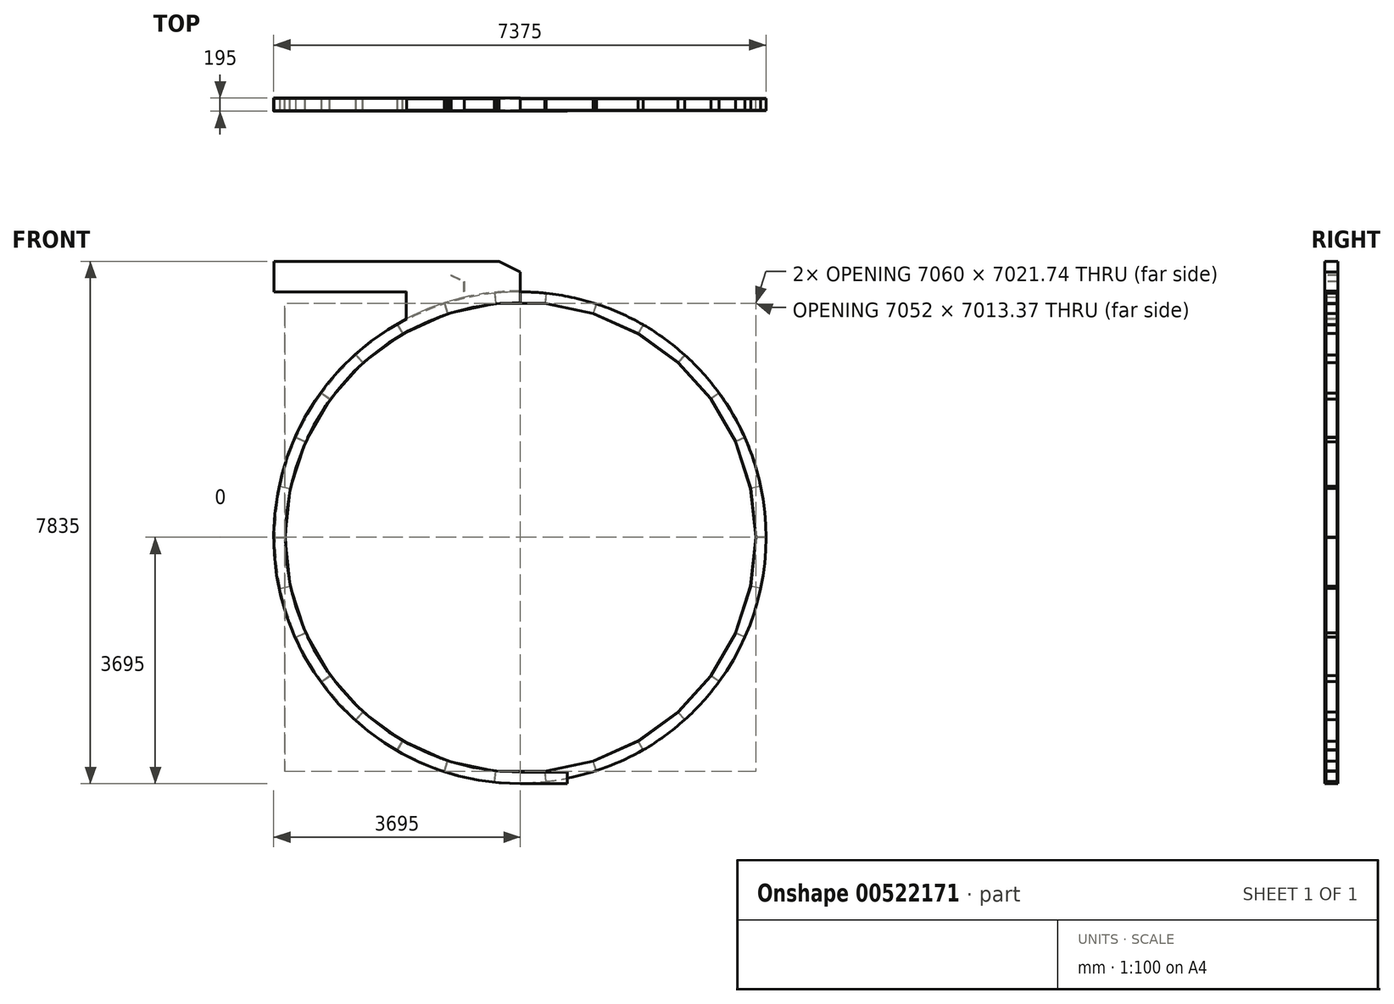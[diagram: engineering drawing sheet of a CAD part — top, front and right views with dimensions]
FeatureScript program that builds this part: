
annotation { "Feature Type Name" : "Feature", "Feature Type Description" : "" }
export const myFeature = defineFeature(function(context is Context, id is Id, definition is map)
    precondition{}
    {
        {
            var Q0;
            Q0=qCreatedBy(makeId("Front.planeOp"),FACE);
            var sketch = newSketch(context, id + "F0", { "sketchPlane" : qUnion([Q0])});
            skCircle(sketch, "E0", {"center": v(0, 0) * mm, "radius": 3680 * mm});
            skPoint(sketch, "E1", {"position": v(-3700, 0) * mm});
            skPoint(sketch, "E2", {"position": v(-3680, 0) * mm});
            skLineSegment(sketch, "E3", {"start": v(-3680, 0) * mm, "end": v(0, 0) * mm, "construction": true});
            skPoint(sketch, "E4", {"position": v(-3530, 0) * mm});
            skLineSegment(sketch, "E5", {"start": v(-3680, 0) * mm, "end": v(-3530, 0) * mm});
            skPoint(sketch, "E6", {"position": v(-3680, 2) * mm});
            skPoint(sketch, "E7", {"position": v(-3680, -2) * mm});
            skLineSegment(sketch, "E8", {"start": v(-3680, 2) * mm, "end": v(-3530, 2) * mm});
            skLineSegment(sketch, "E9", {"start": v(-3680, -2) * mm, "end": v(-3530, -2) * mm});
            skLineSegment(sketch, "E10", {"start": v(-3530, -2) * mm, "end": v(-3530, 2) * mm});
            skPoint(sketch, "E11.1.0", {"position": v(-3599.17, -767.07) * mm});
            skLineSegment(sketch, "E11.1.1", {"start": v(-3599.58, -765.12) * mm, "end": v(-3452.86, -733.93) * mm});
            skLineSegment(sketch, "E11.1.2", {"start": v(-3599.17, -767.07) * mm, "end": v(-3452.45, -735.88) * mm});
            skLineSegment(sketch, "E11.1.3", {"start": v(-3600, -763.16) * mm, "end": v(-3453.28, -731.97) * mm});
            skPoint(sketch, "E11.1.4", {"position": v(-3600, -763.16) * mm});
            skPoint(sketch, "E11.1.5", {"position": v(-3452.86, -733.93) * mm});
            skPoint(sketch, "E11.1.6", {"position": v(-3599.58, -765.12) * mm});
            skLineSegment(sketch, "E11.1.7", {"start": v(-3452.45, -735.88) * mm, "end": v(-3453.28, -731.97) * mm});
            skPoint(sketch, "E11.2.0", {"position": v(-3361.03, -1498.62) * mm});
            skLineSegment(sketch, "E11.2.1", {"start": v(-3361.85, -1496.8) * mm, "end": v(-3224.82, -1435.78) * mm});
            skLineSegment(sketch, "E11.2.2", {"start": v(-3361.03, -1498.62) * mm, "end": v(-3224, -1437.6) * mm});
            skLineSegment(sketch, "E11.2.3", {"start": v(-3362.66, -1494.96) * mm, "end": v(-3225.63, -1433.95) * mm});
            skPoint(sketch, "E11.2.4", {"position": v(-3362.66, -1494.96) * mm});
            skPoint(sketch, "E11.2.5", {"position": v(-3224.82, -1435.78) * mm});
            skPoint(sketch, "E11.2.6", {"position": v(-3361.85, -1496.8) * mm});
            skLineSegment(sketch, "E11.2.7", {"start": v(-3224, -1437.6) * mm, "end": v(-3225.63, -1433.95) * mm});
            skPoint(sketch, "E11.3.0", {"position": v(-2976, -2164.67) * mm});
            skLineSegment(sketch, "E11.3.1", {"start": v(-2977.18, -2163.05) * mm, "end": v(-2855.83, -2074.88) * mm});
            skLineSegment(sketch, "E11.3.2", {"start": v(-2976, -2164.67) * mm, "end": v(-2854.65, -2076.5) * mm});
            skLineSegment(sketch, "E11.3.3", {"start": v(-2978.36, -2161.43) * mm, "end": v(-2857, -2073.26) * mm});
            skPoint(sketch, "E11.3.4", {"position": v(-2978.36, -2161.43) * mm});
            skPoint(sketch, "E11.3.5", {"position": v(-2855.83, -2074.88) * mm});
            skPoint(sketch, "E11.3.6", {"position": v(-2977.18, -2163.05) * mm});
            skLineSegment(sketch, "E11.3.7", {"start": v(-2854.65, -2076.5) * mm, "end": v(-2857, -2073.26) * mm});
            skPoint(sketch, "E11.4.0", {"position": v(-2460.91, -2736.11) * mm});
            skLineSegment(sketch, "E11.4.1", {"start": v(-2462.4, -2734.77) * mm, "end": v(-2362.03, -2623.3) * mm});
            skLineSegment(sketch, "E11.4.2", {"start": v(-2460.91, -2736.11) * mm, "end": v(-2360.54, -2624.64) * mm});
            skLineSegment(sketch, "E11.4.3", {"start": v(-2463.89, -2733.43) * mm, "end": v(-2363.52, -2621.96) * mm});
            skPoint(sketch, "E11.4.4", {"position": v(-2463.89, -2733.43) * mm});
            skPoint(sketch, "E11.4.5", {"position": v(-2362.03, -2623.3) * mm});
            skPoint(sketch, "E11.4.6", {"position": v(-2462.4, -2734.77) * mm});
            skLineSegment(sketch, "E11.4.7", {"start": v(-2360.54, -2624.64) * mm, "end": v(-2363.52, -2621.96) * mm});
            skPoint(sketch, "E11.5.0", {"position": v(-1838.27, -3187.97) * mm});
            skLineSegment(sketch, "E11.5.1", {"start": v(-1840, -3186.97) * mm, "end": v(-1765, -3057.07) * mm});
            skLineSegment(sketch, "E11.5.2", {"start": v(-1838.27, -3187.97) * mm, "end": v(-1763.27, -3058.07) * mm});
            skLineSegment(sketch, "E11.5.3", {"start": v(-1841.73, -3185.97) * mm, "end": v(-1766.73, -3056.07) * mm});
            skPoint(sketch, "E11.5.4", {"position": v(-1841.73, -3185.97) * mm});
            skPoint(sketch, "E11.5.5", {"position": v(-1765, -3057.07) * mm});
            skPoint(sketch, "E11.5.6", {"position": v(-1840, -3186.97) * mm});
            skLineSegment(sketch, "E11.5.7", {"start": v(-1763.27, -3058.07) * mm, "end": v(-1766.73, -3056.07) * mm});
            skPoint(sketch, "E11.6.0", {"position": v(-1135.28, -3500.5) * mm});
            skLineSegment(sketch, "E11.6.1", {"start": v(-1137.18, -3499.89) * mm, "end": v(-1090.83, -3357.23) * mm});
            skLineSegment(sketch, "E11.6.2", {"start": v(-1135.28, -3500.5) * mm, "end": v(-1088.93, -3357.85) * mm});
            skLineSegment(sketch, "E11.6.3", {"start": v(-1139.08, -3499.27) * mm, "end": v(-1092.73, -3356.61) * mm});
            skPoint(sketch, "E11.6.4", {"position": v(-1139.08, -3499.27) * mm});
            skPoint(sketch, "E11.6.5", {"position": v(-1090.83, -3357.23) * mm});
            skPoint(sketch, "E11.6.6", {"position": v(-1137.18, -3499.89) * mm});
            skLineSegment(sketch, "E11.6.7", {"start": v(-1088.93, -3357.85) * mm, "end": v(-1092.73, -3356.61) * mm});
            skPoint(sketch, "E11.7.0", {"position": v(-382.68, -3660.05) * mm});
            skLineSegment(sketch, "E11.7.1", {"start": v(-384.66, -3659.84) * mm, "end": v(-368.99, -3510.66) * mm});
            skLineSegment(sketch, "E11.7.2", {"start": v(-382.68, -3660.05) * mm, "end": v(-367, -3510.87) * mm});
            skLineSegment(sketch, "E11.7.3", {"start": v(-386.65, -3659.63) * mm, "end": v(-370.97, -3510.45) * mm});
            skPoint(sketch, "E11.7.4", {"position": v(-386.65, -3659.63) * mm});
            skPoint(sketch, "E11.7.5", {"position": v(-368.99, -3510.66) * mm});
            skPoint(sketch, "E11.7.6", {"position": v(-384.66, -3659.84) * mm});
            skLineSegment(sketch, "E11.7.7", {"start": v(-367, -3510.87) * mm, "end": v(-370.97, -3510.45) * mm});
            skPoint(sketch, "E11.8.0", {"position": v(386.65, -3659.63) * mm});
            skLineSegment(sketch, "E11.8.1", {"start": v(384.66, -3659.84) * mm, "end": v(368.99, -3510.66) * mm});
            skLineSegment(sketch, "E11.8.2", {"start": v(386.65, -3659.63) * mm, "end": v(370.97, -3510.45) * mm});
            skLineSegment(sketch, "E11.8.3", {"start": v(382.68, -3660.05) * mm, "end": v(367, -3510.87) * mm});
            skPoint(sketch, "E11.8.4", {"position": v(382.68, -3660.05) * mm});
            skPoint(sketch, "E11.8.5", {"position": v(368.99, -3510.66) * mm});
            skPoint(sketch, "E11.8.6", {"position": v(384.66, -3659.84) * mm});
            skLineSegment(sketch, "E11.8.7", {"start": v(370.97, -3510.45) * mm, "end": v(367, -3510.87) * mm});
            skPoint(sketch, "E11.9.0", {"position": v(1139.08, -3499.27) * mm});
            skLineSegment(sketch, "E11.9.1", {"start": v(1137.18, -3499.89) * mm, "end": v(1090.83, -3357.23) * mm});
            skLineSegment(sketch, "E11.9.2", {"start": v(1139.08, -3499.27) * mm, "end": v(1092.73, -3356.61) * mm});
            skLineSegment(sketch, "E11.9.3", {"start": v(1135.28, -3500.5) * mm, "end": v(1088.93, -3357.85) * mm});
            skPoint(sketch, "E11.9.4", {"position": v(1135.28, -3500.5) * mm});
            skPoint(sketch, "E11.9.5", {"position": v(1090.83, -3357.23) * mm});
            skPoint(sketch, "E11.9.6", {"position": v(1137.18, -3499.89) * mm});
            skLineSegment(sketch, "E11.9.7", {"start": v(1092.73, -3356.61) * mm, "end": v(1088.93, -3357.85) * mm});
            skPoint(sketch, "E11.10.0", {"position": v(1841.73, -3185.97) * mm});
            skLineSegment(sketch, "E11.10.1", {"start": v(1840, -3186.97) * mm, "end": v(1765, -3057.07) * mm});
            skLineSegment(sketch, "E11.10.2", {"start": v(1841.73, -3185.97) * mm, "end": v(1766.73, -3056.07) * mm});
            skLineSegment(sketch, "E11.10.3", {"start": v(1838.27, -3187.97) * mm, "end": v(1763.27, -3058.07) * mm});
            skPoint(sketch, "E11.10.4", {"position": v(1838.27, -3187.97) * mm});
            skPoint(sketch, "E11.10.5", {"position": v(1765, -3057.07) * mm});
            skPoint(sketch, "E11.10.6", {"position": v(1840, -3186.97) * mm});
            skLineSegment(sketch, "E11.10.7", {"start": v(1766.73, -3056.07) * mm, "end": v(1763.27, -3058.07) * mm});
            skPoint(sketch, "E11.11.0", {"position": v(2463.89, -2733.43) * mm});
            skLineSegment(sketch, "E11.11.1", {"start": v(2462.4, -2734.77) * mm, "end": v(2362.03, -2623.3) * mm});
            skLineSegment(sketch, "E11.11.2", {"start": v(2463.89, -2733.43) * mm, "end": v(2363.52, -2621.96) * mm});
            skLineSegment(sketch, "E11.11.3", {"start": v(2460.91, -2736.11) * mm, "end": v(2360.54, -2624.64) * mm});
            skPoint(sketch, "E11.11.4", {"position": v(2460.91, -2736.11) * mm});
            skPoint(sketch, "E11.11.5", {"position": v(2362.03, -2623.3) * mm});
            skPoint(sketch, "E11.11.6", {"position": v(2462.4, -2734.77) * mm});
            skLineSegment(sketch, "E11.11.7", {"start": v(2363.52, -2621.96) * mm, "end": v(2360.54, -2624.64) * mm});
            skPoint(sketch, "E11.12.0", {"position": v(2978.36, -2161.43) * mm});
            skLineSegment(sketch, "E11.12.1", {"start": v(2977.18, -2163.05) * mm, "end": v(2855.83, -2074.88) * mm});
            skLineSegment(sketch, "E11.12.2", {"start": v(2978.36, -2161.43) * mm, "end": v(2857, -2073.26) * mm});
            skLineSegment(sketch, "E11.12.3", {"start": v(2976, -2164.67) * mm, "end": v(2854.65, -2076.5) * mm});
            skPoint(sketch, "E11.12.4", {"position": v(2976, -2164.67) * mm});
            skPoint(sketch, "E11.12.5", {"position": v(2855.83, -2074.88) * mm});
            skPoint(sketch, "E11.12.6", {"position": v(2977.18, -2163.05) * mm});
            skLineSegment(sketch, "E11.12.7", {"start": v(2857, -2073.26) * mm, "end": v(2854.65, -2076.5) * mm});
            skPoint(sketch, "E11.13.0", {"position": v(3362.66, -1494.96) * mm});
            skLineSegment(sketch, "E11.13.1", {"start": v(3361.85, -1496.8) * mm, "end": v(3224.82, -1435.78) * mm});
            skLineSegment(sketch, "E11.13.2", {"start": v(3362.66, -1494.96) * mm, "end": v(3225.63, -1433.95) * mm});
            skLineSegment(sketch, "E11.13.3", {"start": v(3361.03, -1498.62) * mm, "end": v(3224, -1437.6) * mm});
            skPoint(sketch, "E11.13.4", {"position": v(3361.03, -1498.62) * mm});
            skPoint(sketch, "E11.13.5", {"position": v(3224.82, -1435.78) * mm});
            skPoint(sketch, "E11.13.6", {"position": v(3361.85, -1496.8) * mm});
            skLineSegment(sketch, "E11.13.7", {"start": v(3225.63, -1433.95) * mm, "end": v(3224, -1437.6) * mm});
            skPoint(sketch, "E11.14.0", {"position": v(3600, -763.16) * mm});
            skLineSegment(sketch, "E11.14.1", {"start": v(3599.58, -765.12) * mm, "end": v(3452.86, -733.93) * mm});
            skLineSegment(sketch, "E11.14.2", {"start": v(3600, -763.16) * mm, "end": v(3453.28, -731.97) * mm});
            skLineSegment(sketch, "E11.14.3", {"start": v(3599.17, -767.07) * mm, "end": v(3452.45, -735.88) * mm});
            skPoint(sketch, "E11.14.4", {"position": v(3599.17, -767.07) * mm});
            skPoint(sketch, "E11.14.5", {"position": v(3452.86, -733.93) * mm});
            skPoint(sketch, "E11.14.6", {"position": v(3599.58, -765.12) * mm});
            skLineSegment(sketch, "E11.14.7", {"start": v(3453.28, -731.97) * mm, "end": v(3452.45, -735.88) * mm});
            skPoint(sketch, "E11.15.0", {"position": v(3680, 2) * mm});
            skLineSegment(sketch, "E11.15.1", {"start": v(3680, 0) * mm, "end": v(3530, 0) * mm});
            skLineSegment(sketch, "E11.15.2", {"start": v(3680, 2) * mm, "end": v(3530, 2) * mm});
            skLineSegment(sketch, "E11.15.3", {"start": v(3680, -2) * mm, "end": v(3530, -2) * mm});
            skPoint(sketch, "E11.15.4", {"position": v(3680, -2) * mm});
            skPoint(sketch, "E11.15.5", {"position": v(3530, 0) * mm});
            skPoint(sketch, "E11.15.6", {"position": v(3680, 0) * mm});
            skLineSegment(sketch, "E11.15.7", {"start": v(3530, 2) * mm, "end": v(3530, -2) * mm});
            skPoint(sketch, "E11.16.0", {"position": v(3599.17, 767.07) * mm});
            skLineSegment(sketch, "E11.16.1", {"start": v(3599.58, 765.12) * mm, "end": v(3452.86, 733.93) * mm});
            skLineSegment(sketch, "E11.16.2", {"start": v(3599.17, 767.07) * mm, "end": v(3452.45, 735.88) * mm});
            skLineSegment(sketch, "E11.16.3", {"start": v(3600, 763.16) * mm, "end": v(3453.28, 731.97) * mm});
            skPoint(sketch, "E11.16.4", {"position": v(3600, 763.16) * mm});
            skPoint(sketch, "E11.16.5", {"position": v(3452.86, 733.93) * mm});
            skPoint(sketch, "E11.16.6", {"position": v(3599.58, 765.12) * mm});
            skLineSegment(sketch, "E11.16.7", {"start": v(3452.45, 735.88) * mm, "end": v(3453.28, 731.97) * mm});
            skPoint(sketch, "E11.17.0", {"position": v(3361.03, 1498.62) * mm});
            skLineSegment(sketch, "E11.17.1", {"start": v(3361.85, 1496.8) * mm, "end": v(3224.82, 1435.78) * mm});
            skLineSegment(sketch, "E11.17.2", {"start": v(3361.03, 1498.62) * mm, "end": v(3224, 1437.6) * mm});
            skLineSegment(sketch, "E11.17.3", {"start": v(3362.66, 1494.96) * mm, "end": v(3225.63, 1433.95) * mm});
            skPoint(sketch, "E11.17.4", {"position": v(3362.66, 1494.96) * mm});
            skPoint(sketch, "E11.17.5", {"position": v(3224.82, 1435.78) * mm});
            skPoint(sketch, "E11.17.6", {"position": v(3361.85, 1496.8) * mm});
            skLineSegment(sketch, "E11.17.7", {"start": v(3224, 1437.6) * mm, "end": v(3225.63, 1433.95) * mm});
            skPoint(sketch, "E11.18.0", {"position": v(2976, 2164.67) * mm});
            skLineSegment(sketch, "E11.18.1", {"start": v(2977.18, 2163.05) * mm, "end": v(2855.83, 2074.88) * mm});
            skLineSegment(sketch, "E11.18.2", {"start": v(2976, 2164.67) * mm, "end": v(2854.65, 2076.5) * mm});
            skLineSegment(sketch, "E11.18.3", {"start": v(2978.36, 2161.43) * mm, "end": v(2857, 2073.26) * mm});
            skPoint(sketch, "E11.18.4", {"position": v(2978.36, 2161.43) * mm});
            skPoint(sketch, "E11.18.5", {"position": v(2855.83, 2074.88) * mm});
            skPoint(sketch, "E11.18.6", {"position": v(2977.18, 2163.05) * mm});
            skLineSegment(sketch, "E11.18.7", {"start": v(2854.65, 2076.5) * mm, "end": v(2857, 2073.26) * mm});
            skPoint(sketch, "E11.19.0", {"position": v(2460.91, 2736.11) * mm});
            skLineSegment(sketch, "E11.19.1", {"start": v(2462.4, 2734.77) * mm, "end": v(2362.03, 2623.3) * mm});
            skLineSegment(sketch, "E11.19.2", {"start": v(2460.91, 2736.11) * mm, "end": v(2360.54, 2624.64) * mm});
            skLineSegment(sketch, "E11.19.3", {"start": v(2463.89, 2733.43) * mm, "end": v(2363.52, 2621.96) * mm});
            skPoint(sketch, "E11.19.4", {"position": v(2463.89, 2733.43) * mm});
            skPoint(sketch, "E11.19.5", {"position": v(2362.03, 2623.3) * mm});
            skPoint(sketch, "E11.19.6", {"position": v(2462.4, 2734.77) * mm});
            skLineSegment(sketch, "E11.19.7", {"start": v(2360.54, 2624.64) * mm, "end": v(2363.52, 2621.96) * mm});
            skPoint(sketch, "E11.20.0", {"position": v(1838.27, 3187.97) * mm});
            skLineSegment(sketch, "E11.20.1", {"start": v(1840, 3186.97) * mm, "end": v(1765, 3057.07) * mm});
            skLineSegment(sketch, "E11.20.2", {"start": v(1838.27, 3187.97) * mm, "end": v(1763.27, 3058.07) * mm});
            skLineSegment(sketch, "E11.20.3", {"start": v(1841.73, 3185.97) * mm, "end": v(1766.73, 3056.07) * mm});
            skPoint(sketch, "E11.20.4", {"position": v(1841.73, 3185.97) * mm});
            skPoint(sketch, "E11.20.5", {"position": v(1765, 3057.07) * mm});
            skPoint(sketch, "E11.20.6", {"position": v(1840, 3186.97) * mm});
            skLineSegment(sketch, "E11.20.7", {"start": v(1763.27, 3058.07) * mm, "end": v(1766.73, 3056.07) * mm});
            skPoint(sketch, "E11.21.0", {"position": v(1135.28, 3500.5) * mm});
            skLineSegment(sketch, "E11.21.1", {"start": v(1137.18, 3499.89) * mm, "end": v(1090.83, 3357.23) * mm});
            skLineSegment(sketch, "E11.21.2", {"start": v(1135.28, 3500.5) * mm, "end": v(1088.93, 3357.85) * mm});
            skLineSegment(sketch, "E11.21.3", {"start": v(1139.08, 3499.27) * mm, "end": v(1092.73, 3356.61) * mm});
            skPoint(sketch, "E11.21.4", {"position": v(1139.08, 3499.27) * mm});
            skPoint(sketch, "E11.21.5", {"position": v(1090.83, 3357.23) * mm});
            skPoint(sketch, "E11.21.6", {"position": v(1137.18, 3499.89) * mm});
            skLineSegment(sketch, "E11.21.7", {"start": v(1088.93, 3357.85) * mm, "end": v(1092.73, 3356.61) * mm});
            skPoint(sketch, "E11.22.0", {"position": v(382.68, 3660.05) * mm});
            skLineSegment(sketch, "E11.22.1", {"start": v(384.66, 3659.84) * mm, "end": v(368.99, 3510.66) * mm});
            skLineSegment(sketch, "E11.22.2", {"start": v(382.68, 3660.05) * mm, "end": v(367, 3510.87) * mm});
            skLineSegment(sketch, "E11.22.3", {"start": v(386.65, 3659.63) * mm, "end": v(370.97, 3510.45) * mm});
            skPoint(sketch, "E11.22.4", {"position": v(386.65, 3659.63) * mm});
            skPoint(sketch, "E11.22.5", {"position": v(368.99, 3510.66) * mm});
            skPoint(sketch, "E11.22.6", {"position": v(384.66, 3659.84) * mm});
            skLineSegment(sketch, "E11.22.7", {"start": v(367, 3510.87) * mm, "end": v(370.97, 3510.45) * mm});
            skPoint(sketch, "E11.23.0", {"position": v(-386.65, 3659.63) * mm});
            skLineSegment(sketch, "E11.23.1", {"start": v(-384.66, 3659.84) * mm, "end": v(-368.99, 3510.66) * mm});
            skLineSegment(sketch, "E11.23.2", {"start": v(-386.65, 3659.63) * mm, "end": v(-370.97, 3510.45) * mm});
            skLineSegment(sketch, "E11.23.3", {"start": v(-382.68, 3660.05) * mm, "end": v(-367, 3510.87) * mm});
            skPoint(sketch, "E11.23.4", {"position": v(-382.68, 3660.05) * mm});
            skPoint(sketch, "E11.23.5", {"position": v(-368.99, 3510.66) * mm});
            skPoint(sketch, "E11.23.6", {"position": v(-384.66, 3659.84) * mm});
            skLineSegment(sketch, "E11.23.7", {"start": v(-370.97, 3510.45) * mm, "end": v(-367, 3510.87) * mm});
            skPoint(sketch, "E11.24.0", {"position": v(-1139.08, 3499.27) * mm});
            skLineSegment(sketch, "E11.24.1", {"start": v(-1137.18, 3499.89) * mm, "end": v(-1090.83, 3357.23) * mm});
            skLineSegment(sketch, "E11.24.2", {"start": v(-1139.08, 3499.27) * mm, "end": v(-1092.73, 3356.61) * mm});
            skLineSegment(sketch, "E11.24.3", {"start": v(-1135.28, 3500.5) * mm, "end": v(-1088.93, 3357.85) * mm});
            skPoint(sketch, "E11.24.4", {"position": v(-1135.28, 3500.5) * mm});
            skPoint(sketch, "E11.24.5", {"position": v(-1090.83, 3357.23) * mm});
            skPoint(sketch, "E11.24.6", {"position": v(-1137.18, 3499.89) * mm});
            skLineSegment(sketch, "E11.24.7", {"start": v(-1092.73, 3356.61) * mm, "end": v(-1088.93, 3357.85) * mm});
            skPoint(sketch, "E11.25.0", {"position": v(-1841.73, 3185.97) * mm});
            skLineSegment(sketch, "E11.25.1", {"start": v(-1840, 3186.97) * mm, "end": v(-1765, 3057.07) * mm});
            skLineSegment(sketch, "E11.25.2", {"start": v(-1841.73, 3185.97) * mm, "end": v(-1766.73, 3056.07) * mm});
            skLineSegment(sketch, "E11.25.3", {"start": v(-1838.27, 3187.97) * mm, "end": v(-1763.27, 3058.07) * mm});
            skPoint(sketch, "E11.25.4", {"position": v(-1838.27, 3187.97) * mm});
            skPoint(sketch, "E11.25.5", {"position": v(-1765, 3057.07) * mm});
            skPoint(sketch, "E11.25.6", {"position": v(-1840, 3186.97) * mm});
            skLineSegment(sketch, "E11.25.7", {"start": v(-1766.73, 3056.07) * mm, "end": v(-1763.27, 3058.07) * mm});
            skPoint(sketch, "E11.26.0", {"position": v(-2463.89, 2733.43) * mm});
            skLineSegment(sketch, "E11.26.1", {"start": v(-2462.4, 2734.77) * mm, "end": v(-2362.03, 2623.3) * mm});
            skLineSegment(sketch, "E11.26.2", {"start": v(-2463.89, 2733.43) * mm, "end": v(-2363.52, 2621.96) * mm});
            skLineSegment(sketch, "E11.26.3", {"start": v(-2460.91, 2736.11) * mm, "end": v(-2360.54, 2624.64) * mm});
            skPoint(sketch, "E11.26.4", {"position": v(-2460.91, 2736.11) * mm});
            skPoint(sketch, "E11.26.5", {"position": v(-2362.03, 2623.3) * mm});
            skPoint(sketch, "E11.26.6", {"position": v(-2462.4, 2734.77) * mm});
            skLineSegment(sketch, "E11.26.7", {"start": v(-2363.52, 2621.96) * mm, "end": v(-2360.54, 2624.64) * mm});
            skPoint(sketch, "E11.27.0", {"position": v(-2978.36, 2161.43) * mm});
            skLineSegment(sketch, "E11.27.1", {"start": v(-2977.18, 2163.05) * mm, "end": v(-2855.83, 2074.88) * mm});
            skLineSegment(sketch, "E11.27.2", {"start": v(-2978.36, 2161.43) * mm, "end": v(-2857, 2073.26) * mm});
            skLineSegment(sketch, "E11.27.3", {"start": v(-2976, 2164.67) * mm, "end": v(-2854.65, 2076.5) * mm});
            skPoint(sketch, "E11.27.4", {"position": v(-2976, 2164.67) * mm});
            skPoint(sketch, "E11.27.5", {"position": v(-2855.83, 2074.88) * mm});
            skPoint(sketch, "E11.27.6", {"position": v(-2977.18, 2163.05) * mm});
            skLineSegment(sketch, "E11.27.7", {"start": v(-2857, 2073.26) * mm, "end": v(-2854.65, 2076.5) * mm});
            skPoint(sketch, "E11.28.0", {"position": v(-3362.66, 1494.96) * mm});
            skLineSegment(sketch, "E11.28.1", {"start": v(-3361.85, 1496.8) * mm, "end": v(-3224.82, 1435.78) * mm});
            skLineSegment(sketch, "E11.28.2", {"start": v(-3362.66, 1494.96) * mm, "end": v(-3225.63, 1433.95) * mm});
            skLineSegment(sketch, "E11.28.3", {"start": v(-3361.03, 1498.62) * mm, "end": v(-3224, 1437.6) * mm});
            skPoint(sketch, "E11.28.4", {"position": v(-3361.03, 1498.62) * mm});
            skPoint(sketch, "E11.28.5", {"position": v(-3224.82, 1435.78) * mm});
            skPoint(sketch, "E11.28.6", {"position": v(-3361.85, 1496.8) * mm});
            skLineSegment(sketch, "E11.28.7", {"start": v(-3225.63, 1433.95) * mm, "end": v(-3224, 1437.6) * mm});
            skPoint(sketch, "E11.29.0", {"position": v(-3600, 763.16) * mm});
            skLineSegment(sketch, "E11.29.1", {"start": v(-3599.58, 765.12) * mm, "end": v(-3452.86, 733.93) * mm});
            skLineSegment(sketch, "E11.29.2", {"start": v(-3600, 763.16) * mm, "end": v(-3453.28, 731.97) * mm});
            skLineSegment(sketch, "E11.29.3", {"start": v(-3599.17, 767.07) * mm, "end": v(-3452.45, 735.88) * mm});
            skPoint(sketch, "E11.29.4", {"position": v(-3599.17, 767.07) * mm});
            skPoint(sketch, "E11.29.5", {"position": v(-3452.86, 733.93) * mm});
            skPoint(sketch, "E11.29.6", {"position": v(-3599.58, 765.12) * mm});
            skLineSegment(sketch, "E11.29.7", {"start": v(-3453.28, 731.97) * mm, "end": v(-3452.45, 735.88) * mm});
            skLineSegment(sketch, "E12", {"start": v(-3453.28, 731.97) * mm, "end": v(-3530, 2) * mm});
            skLineSegment(sketch, "E13", {"start": v(-3452.86, 733.93) * mm, "end": v(-3445.57, 732.38) * mm, "construction": true});
            skPoint(sketch, "E14", {"position": v(-3526, 0) * mm});
            skLineSegment(sketch, "E15", {"start": v(-3526, 0) * mm, "end": v(-3448.95, 733.1) * mm});
            skLineSegment(sketch, "E16.1.0", {"start": v(-3530, -2) * mm, "end": v(-3453.28, -731.97) * mm});
            skLineSegment(sketch, "E16.1.1", {"start": v(-3448.95, -733.1) * mm, "end": v(-3526, 0) * mm});
            skLineSegment(sketch, "E16.1.2", {"start": v(-3530, 0) * mm, "end": v(-3522.54, 0) * mm, "construction": true});
            skLineSegment(sketch, "E16.2.0", {"start": v(-3452.45, -735.88) * mm, "end": v(-3225.63, -1433.95) * mm});
            skLineSegment(sketch, "E16.2.1", {"start": v(-3221.16, -1434.15) * mm, "end": v(-3448.95, -733.1) * mm});
            skLineSegment(sketch, "E16.2.2", {"start": v(-3452.86, -733.93) * mm, "end": v(-3445.57, -732.38) * mm, "construction": true});
            skLineSegment(sketch, "E16.3.0", {"start": v(-3224, -1437.6) * mm, "end": v(-2857, -2073.26) * mm});
            skLineSegment(sketch, "E16.3.1", {"start": v(-2852.6, -2072.53) * mm, "end": v(-3221.16, -1434.15) * mm});
            skLineSegment(sketch, "E16.3.2", {"start": v(-3224.82, -1435.78) * mm, "end": v(-3218, -1432.75) * mm, "construction": true});
            skLineSegment(sketch, "E16.4.0", {"start": v(-2854.65, -2076.5) * mm, "end": v(-2363.52, -2621.96) * mm});
            skLineSegment(sketch, "E16.4.1", {"start": v(-2359.35, -2620.33) * mm, "end": v(-2852.6, -2072.53) * mm});
            skLineSegment(sketch, "E16.4.2", {"start": v(-2855.83, -2074.88) * mm, "end": v(-2849.8, -2070.5) * mm, "construction": true});
            skLineSegment(sketch, "E16.5.0", {"start": v(-2360.54, -2624.64) * mm, "end": v(-1766.73, -3056.07) * mm});
            skLineSegment(sketch, "E16.5.1", {"start": v(-1763, -3053.6) * mm, "end": v(-2359.35, -2620.33) * mm});
            skLineSegment(sketch, "E16.5.2", {"start": v(-2362.03, -2623.3) * mm, "end": v(-2357.04, -2617.76) * mm, "construction": true});
            skLineSegment(sketch, "E16.6.0", {"start": v(-1763.27, -3058.07) * mm, "end": v(-1092.73, -3356.61) * mm});
            skLineSegment(sketch, "E16.6.1", {"start": v(-1089.6, -3353.43) * mm, "end": v(-1763, -3053.6) * mm});
            skLineSegment(sketch, "E16.6.2", {"start": v(-1765, -3057.07) * mm, "end": v(-1761.27, -3050.61) * mm, "construction": true});
            skLineSegment(sketch, "E16.7.0", {"start": v(-1088.93, -3357.85) * mm, "end": v(-370.97, -3510.45) * mm});
            skLineSegment(sketch, "E16.7.1", {"start": v(-368.57, -3506.68) * mm, "end": v(-1089.6, -3353.43) * mm});
            skLineSegment(sketch, "E16.7.2", {"start": v(-1090.83, -3357.23) * mm, "end": v(-1088.53, -3350.14) * mm, "construction": true});
            skLineSegment(sketch, "E16.8.0", {"start": v(-367, -3510.87) * mm, "end": v(367, -3510.87) * mm});
            skLineSegment(sketch, "E16.8.1", {"start": v(368.57, -3506.68) * mm, "end": v(-368.57, -3506.68) * mm});
            skLineSegment(sketch, "E16.8.2", {"start": v(-368.99, -3510.66) * mm, "end": v(-368.2, -3503.25) * mm, "construction": true});
            skLineSegment(sketch, "E16.9.0", {"start": v(370.97, -3510.45) * mm, "end": v(1088.93, -3357.85) * mm});
            skLineSegment(sketch, "E16.9.1", {"start": v(1089.6, -3353.43) * mm, "end": v(368.57, -3506.68) * mm});
            skLineSegment(sketch, "E16.9.2", {"start": v(368.99, -3510.66) * mm, "end": v(368.2, -3503.25) * mm, "construction": true});
            skLineSegment(sketch, "E16.10.0", {"start": v(1092.73, -3356.61) * mm, "end": v(1763.27, -3058.07) * mm});
            skLineSegment(sketch, "E16.10.1", {"start": v(1763, -3053.6) * mm, "end": v(1089.6, -3353.43) * mm});
            skLineSegment(sketch, "E16.10.2", {"start": v(1090.83, -3357.23) * mm, "end": v(1088.53, -3350.14) * mm, "construction": true});
            skLineSegment(sketch, "E16.11.0", {"start": v(1766.73, -3056.07) * mm, "end": v(2360.54, -2624.64) * mm});
            skLineSegment(sketch, "E16.11.1", {"start": v(2359.35, -2620.33) * mm, "end": v(1763, -3053.6) * mm});
            skLineSegment(sketch, "E16.11.2", {"start": v(1765, -3057.07) * mm, "end": v(1761.27, -3050.61) * mm, "construction": true});
            skLineSegment(sketch, "E16.12.0", {"start": v(2363.52, -2621.96) * mm, "end": v(2854.65, -2076.5) * mm});
            skLineSegment(sketch, "E16.12.1", {"start": v(2852.6, -2072.53) * mm, "end": v(2359.35, -2620.33) * mm});
            skLineSegment(sketch, "E16.12.2", {"start": v(2362.03, -2623.3) * mm, "end": v(2357.04, -2617.76) * mm, "construction": true});
            skLineSegment(sketch, "E16.13.0", {"start": v(2857, -2073.26) * mm, "end": v(3224, -1437.6) * mm});
            skLineSegment(sketch, "E16.13.1", {"start": v(3221.16, -1434.15) * mm, "end": v(2852.6, -2072.53) * mm});
            skLineSegment(sketch, "E16.13.2", {"start": v(2855.83, -2074.88) * mm, "end": v(2849.8, -2070.5) * mm, "construction": true});
            skLineSegment(sketch, "E16.14.0", {"start": v(3225.63, -1433.95) * mm, "end": v(3452.45, -735.88) * mm});
            skLineSegment(sketch, "E16.14.1", {"start": v(3448.95, -733.1) * mm, "end": v(3221.16, -1434.15) * mm});
            skLineSegment(sketch, "E16.14.2", {"start": v(3224.82, -1435.78) * mm, "end": v(3218, -1432.75) * mm, "construction": true});
            skLineSegment(sketch, "E16.15.0", {"start": v(3453.28, -731.97) * mm, "end": v(3530, -2) * mm});
            skLineSegment(sketch, "E16.15.1", {"start": v(3526, 0) * mm, "end": v(3448.95, -733.1) * mm});
            skLineSegment(sketch, "E16.15.2", {"start": v(3452.86, -733.93) * mm, "end": v(3445.57, -732.38) * mm, "construction": true});
            skLineSegment(sketch, "E16.16.0", {"start": v(3530, 2) * mm, "end": v(3453.28, 731.97) * mm});
            skLineSegment(sketch, "E16.16.1", {"start": v(3448.95, 733.1) * mm, "end": v(3526, 0) * mm});
            skLineSegment(sketch, "E16.16.2", {"start": v(3530, 0) * mm, "end": v(3522.54, 0) * mm, "construction": true});
            skLineSegment(sketch, "E16.17.0", {"start": v(3452.45, 735.88) * mm, "end": v(3225.63, 1433.95) * mm});
            skLineSegment(sketch, "E16.17.1", {"start": v(3221.16, 1434.15) * mm, "end": v(3448.95, 733.1) * mm});
            skLineSegment(sketch, "E16.17.2", {"start": v(3452.86, 733.93) * mm, "end": v(3445.57, 732.38) * mm, "construction": true});
            skLineSegment(sketch, "E16.18.0", {"start": v(3224, 1437.6) * mm, "end": v(2857, 2073.26) * mm});
            skLineSegment(sketch, "E16.18.1", {"start": v(2852.6, 2072.53) * mm, "end": v(3221.16, 1434.15) * mm});
            skLineSegment(sketch, "E16.18.2", {"start": v(3224.82, 1435.78) * mm, "end": v(3218, 1432.75) * mm, "construction": true});
            skLineSegment(sketch, "E16.19.0", {"start": v(2854.65, 2076.5) * mm, "end": v(2363.52, 2621.96) * mm});
            skLineSegment(sketch, "E16.19.1", {"start": v(2359.35, 2620.33) * mm, "end": v(2852.6, 2072.53) * mm});
            skLineSegment(sketch, "E16.19.2", {"start": v(2855.83, 2074.88) * mm, "end": v(2849.8, 2070.5) * mm, "construction": true});
            skLineSegment(sketch, "E16.20.0", {"start": v(2360.54, 2624.64) * mm, "end": v(1766.73, 3056.07) * mm});
            skLineSegment(sketch, "E16.20.1", {"start": v(1763, 3053.6) * mm, "end": v(2359.35, 2620.33) * mm});
            skLineSegment(sketch, "E16.20.2", {"start": v(2362.03, 2623.3) * mm, "end": v(2357.04, 2617.76) * mm, "construction": true});
            skLineSegment(sketch, "E16.21.0", {"start": v(1763.27, 3058.07) * mm, "end": v(1092.73, 3356.61) * mm});
            skLineSegment(sketch, "E16.21.1", {"start": v(1089.6, 3353.43) * mm, "end": v(1763, 3053.6) * mm});
            skLineSegment(sketch, "E16.21.2", {"start": v(1765, 3057.07) * mm, "end": v(1761.27, 3050.61) * mm, "construction": true});
            skLineSegment(sketch, "E16.22.0", {"start": v(1088.93, 3357.85) * mm, "end": v(370.97, 3510.45) * mm});
            skLineSegment(sketch, "E16.22.1", {"start": v(368.57, 3506.68) * mm, "end": v(1089.6, 3353.43) * mm});
            skLineSegment(sketch, "E16.22.2", {"start": v(1090.83, 3357.23) * mm, "end": v(1088.53, 3350.14) * mm, "construction": true});
            skLineSegment(sketch, "E16.23.0", {"start": v(367, 3510.87) * mm, "end": v(-367, 3510.87) * mm});
            skLineSegment(sketch, "E16.23.1", {"start": v(-368.57, 3506.68) * mm, "end": v(368.57, 3506.68) * mm});
            skLineSegment(sketch, "E16.23.2", {"start": v(368.99, 3510.66) * mm, "end": v(368.2, 3503.25) * mm, "construction": true});
            skLineSegment(sketch, "E16.24.0", {"start": v(-370.97, 3510.45) * mm, "end": v(-1088.93, 3357.85) * mm});
            skLineSegment(sketch, "E16.24.1", {"start": v(-1089.6, 3353.43) * mm, "end": v(-368.57, 3506.68) * mm});
            skLineSegment(sketch, "E16.24.2", {"start": v(-368.99, 3510.66) * mm, "end": v(-368.2, 3503.25) * mm, "construction": true});
            skLineSegment(sketch, "E16.25.0", {"start": v(-1092.73, 3356.61) * mm, "end": v(-1763.27, 3058.07) * mm});
            skLineSegment(sketch, "E16.25.1", {"start": v(-1763, 3053.6) * mm, "end": v(-1089.6, 3353.43) * mm});
            skLineSegment(sketch, "E16.25.2", {"start": v(-1090.83, 3357.23) * mm, "end": v(-1088.53, 3350.14) * mm, "construction": true});
            skLineSegment(sketch, "E16.26.0", {"start": v(-1766.73, 3056.07) * mm, "end": v(-2360.54, 2624.64) * mm});
            skLineSegment(sketch, "E16.26.1", {"start": v(-2359.35, 2620.33) * mm, "end": v(-1763, 3053.6) * mm});
            skLineSegment(sketch, "E16.26.2", {"start": v(-1765, 3057.07) * mm, "end": v(-1761.27, 3050.61) * mm, "construction": true});
            skLineSegment(sketch, "E16.27.0", {"start": v(-2363.52, 2621.96) * mm, "end": v(-2854.65, 2076.5) * mm});
            skLineSegment(sketch, "E16.27.1", {"start": v(-2852.6, 2072.53) * mm, "end": v(-2359.35, 2620.33) * mm});
            skLineSegment(sketch, "E16.27.2", {"start": v(-2362.03, 2623.3) * mm, "end": v(-2357.04, 2617.76) * mm, "construction": true});
            skLineSegment(sketch, "E16.28.0", {"start": v(-2857, 2073.26) * mm, "end": v(-3224, 1437.6) * mm});
            skLineSegment(sketch, "E16.28.1", {"start": v(-3221.16, 1434.15) * mm, "end": v(-2852.6, 2072.53) * mm});
            skLineSegment(sketch, "E16.28.2", {"start": v(-2855.83, 2074.88) * mm, "end": v(-2849.8, 2070.5) * mm, "construction": true});
            skLineSegment(sketch, "E16.29.0", {"start": v(-3225.63, 1433.95) * mm, "end": v(-3452.45, 735.88) * mm});
            skLineSegment(sketch, "E16.29.1", {"start": v(-3448.95, 733.1) * mm, "end": v(-3221.16, 1434.15) * mm});
            skLineSegment(sketch, "E16.29.2", {"start": v(-3224.82, 1435.78) * mm, "end": v(-3218, 1432.75) * mm, "construction": true});
            skSolve(sketch);
        }
        {
            var Q0;
            {var subQ0=sQuery(id+"F0.wireOp",EDGE,"E5");Q0=makeQuery(id+"F0.imprint","IMPRINT",FACE,{"disambiguationData":[TD([[makeQuery(id+"F0.imprint","IMPRINT",EDGE,{"derivedFrom":subQ0}),-1.0]])]});}
            var Q1;
            {var subQ0=sQuery(id+"F0.wireOp",EDGE,"E5");Q1=makeQuery(id+"F0.imprint","IMPRINT",FACE,{"disambiguationData":[TD([[makeQuery(id+"F0.imprint","IMPRINT",EDGE,{"derivedFrom":subQ0}),1.0]])]});}
            var Q2;
            {var subQ14=sQuery(id+"F0.wireOp",EDGE,"E12");Q2=makeQuery(id+"F0.imprint","IMPRINT",FACE,{"disambiguationData":[TD([[makeQuery(id+"F0.imprint","IMPRINT",EDGE,{"derivedFrom":subQ14}),1.0]])]});}
            var Q3;
            {var subQ0=sQuery(id+"F0.wireOp",EDGE,"E11.29.1");Q3=makeQuery(id+"F0.imprint","IMPRINT",FACE,{"disambiguationData":[TD([[makeQuery(id+"F0.imprint","IMPRINT",EDGE,{"derivedFrom":subQ0}),1.0]])]});}
            var Q4;
            {var subQ0=sQuery(id+"F0.wireOp",EDGE,"E11.29.1");Q4=makeQuery(id+"F0.imprint","IMPRINT",FACE,{"disambiguationData":[TD([[makeQuery(id+"F0.imprint","IMPRINT",EDGE,{"derivedFrom":subQ0}),-1.0]])]});}
            var Q5;
            {var subQ0=sQuery(id+"F0.wireOp",EDGE,"E11.28.1");Q5=makeQuery(id+"F0.imprint","IMPRINT",FACE,{"disambiguationData":[TD([[makeQuery(id+"F0.imprint","IMPRINT",EDGE,{"derivedFrom":subQ0}),1.0]])]});}
            var Q6;
            {var subQ0=sQuery(id+"F0.wireOp",EDGE,"E11.28.1");Q6=makeQuery(id+"F0.imprint","IMPRINT",FACE,{"disambiguationData":[TD([[makeQuery(id+"F0.imprint","IMPRINT",EDGE,{"derivedFrom":subQ0}),-1.0]])]});}
            var Q7;
            {var subQ0=sQuery(id+"F0.wireOp",EDGE,"E11.26.1");Q7=makeQuery(id+"F0.imprint","IMPRINT",FACE,{"disambiguationData":[TD([[makeQuery(id+"F0.imprint","IMPRINT",EDGE,{"derivedFrom":subQ0}),1.0]])]});}
            var Q8;
            {var subQ0=sQuery(id+"F0.wireOp",EDGE,"E11.26.1");Q8=makeQuery(id+"F0.imprint","IMPRINT",FACE,{"disambiguationData":[TD([[makeQuery(id+"F0.imprint","IMPRINT",EDGE,{"derivedFrom":subQ0}),-1.0]])]});}
            var Q9;
            {var subQ0=sQuery(id+"F0.wireOp",EDGE,"E11.27.1");Q9=makeQuery(id+"F0.imprint","IMPRINT",FACE,{"disambiguationData":[TD([[makeQuery(id+"F0.imprint","IMPRINT",EDGE,{"derivedFrom":subQ0}),1.0]])]});}
            var Q10;
            {var subQ0=sQuery(id+"F0.wireOp",EDGE,"E11.27.1");Q10=makeQuery(id+"F0.imprint","IMPRINT",FACE,{"disambiguationData":[TD([[makeQuery(id+"F0.imprint","IMPRINT",EDGE,{"derivedFrom":subQ0}),-1.0]])]});}
            var Q11;
            {var subQ0=sQuery(id+"F0.wireOp",EDGE,"E11.25.1");Q11=makeQuery(id+"F0.imprint","IMPRINT",FACE,{"disambiguationData":[TD([[makeQuery(id+"F0.imprint","IMPRINT",EDGE,{"derivedFrom":subQ0}),1.0]])]});}
            var Q12;
            {var subQ0=sQuery(id+"F0.wireOp",EDGE,"E11.25.1");Q12=makeQuery(id+"F0.imprint","IMPRINT",FACE,{"disambiguationData":[TD([[makeQuery(id+"F0.imprint","IMPRINT",EDGE,{"derivedFrom":subQ0}),-1.0]])]});}
            var Q13;
            {var subQ0=sQuery(id+"F0.wireOp",EDGE,"E11.24.1");Q13=makeQuery(id+"F0.imprint","IMPRINT",FACE,{"disambiguationData":[TD([[makeQuery(id+"F0.imprint","IMPRINT",EDGE,{"derivedFrom":subQ0}),1.0]])]});}
            var Q14;
            {var subQ0=sQuery(id+"F0.wireOp",EDGE,"E11.24.1");Q14=makeQuery(id+"F0.imprint","IMPRINT",FACE,{"disambiguationData":[TD([[makeQuery(id+"F0.imprint","IMPRINT",EDGE,{"derivedFrom":subQ0}),-1.0]])]});}
            var Q15;
            {var subQ0=sQuery(id+"F0.wireOp",EDGE,"E11.23.1");Q15=makeQuery(id+"F0.imprint","IMPRINT",FACE,{"disambiguationData":[TD([[makeQuery(id+"F0.imprint","IMPRINT",EDGE,{"derivedFrom":subQ0}),-1.0]])]});}
            var Q16;
            {var subQ0=sQuery(id+"F0.wireOp",EDGE,"E11.23.1");Q16=makeQuery(id+"F0.imprint","IMPRINT",FACE,{"disambiguationData":[TD([[makeQuery(id+"F0.imprint","IMPRINT",EDGE,{"derivedFrom":subQ0}),1.0]])]});}
            var Q17;
            {var subQ0=sQuery(id+"F0.wireOp",EDGE,"E11.22.1");Q17=makeQuery(id+"F0.imprint","IMPRINT",FACE,{"disambiguationData":[TD([[makeQuery(id+"F0.imprint","IMPRINT",EDGE,{"derivedFrom":subQ0}),1.0]])]});}
            var Q18;
            {var subQ0=sQuery(id+"F0.wireOp",EDGE,"E11.22.1");Q18=makeQuery(id+"F0.imprint","IMPRINT",FACE,{"disambiguationData":[TD([[makeQuery(id+"F0.imprint","IMPRINT",EDGE,{"derivedFrom":subQ0}),-1.0]])]});}
            var Q19;
            {var subQ0=sQuery(id+"F0.wireOp",EDGE,"E11.21.1");Q19=makeQuery(id+"F0.imprint","IMPRINT",FACE,{"disambiguationData":[TD([[makeQuery(id+"F0.imprint","IMPRINT",EDGE,{"derivedFrom":subQ0}),1.0]])]});}
            var Q20;
            {var subQ0=sQuery(id+"F0.wireOp",EDGE,"E11.21.1");Q20=makeQuery(id+"F0.imprint","IMPRINT",FACE,{"disambiguationData":[TD([[makeQuery(id+"F0.imprint","IMPRINT",EDGE,{"derivedFrom":subQ0}),-1.0]])]});}
            var Q21;
            {var subQ0=sQuery(id+"F0.wireOp",EDGE,"E11.20.1");Q21=makeQuery(id+"F0.imprint","IMPRINT",FACE,{"disambiguationData":[TD([[makeQuery(id+"F0.imprint","IMPRINT",EDGE,{"derivedFrom":subQ0}),1.0]])]});}
            var Q22;
            {var subQ0=sQuery(id+"F0.wireOp",EDGE,"E11.20.1");Q22=makeQuery(id+"F0.imprint","IMPRINT",FACE,{"disambiguationData":[TD([[makeQuery(id+"F0.imprint","IMPRINT",EDGE,{"derivedFrom":subQ0}),-1.0]])]});}
            var Q23;
            {var subQ0=sQuery(id+"F0.wireOp",EDGE,"E11.19.1");Q23=makeQuery(id+"F0.imprint","IMPRINT",FACE,{"disambiguationData":[TD([[makeQuery(id+"F0.imprint","IMPRINT",EDGE,{"derivedFrom":subQ0}),1.0]])]});}
            var Q24;
            {var subQ0=sQuery(id+"F0.wireOp",EDGE,"E11.19.1");Q24=makeQuery(id+"F0.imprint","IMPRINT",FACE,{"disambiguationData":[TD([[makeQuery(id+"F0.imprint","IMPRINT",EDGE,{"derivedFrom":subQ0}),-1.0]])]});}
            var Q25;
            {var subQ0=sQuery(id+"F0.wireOp",EDGE,"E11.18.1");Q25=makeQuery(id+"F0.imprint","IMPRINT",FACE,{"disambiguationData":[TD([[makeQuery(id+"F0.imprint","IMPRINT",EDGE,{"derivedFrom":subQ0}),1.0]])]});}
            var Q26;
            {var subQ0=sQuery(id+"F0.wireOp",EDGE,"E11.18.1");Q26=makeQuery(id+"F0.imprint","IMPRINT",FACE,{"disambiguationData":[TD([[makeQuery(id+"F0.imprint","IMPRINT",EDGE,{"derivedFrom":subQ0}),-1.0]])]});}
            var Q27;
            {var subQ0=sQuery(id+"F0.wireOp",EDGE,"E11.17.1");Q27=makeQuery(id+"F0.imprint","IMPRINT",FACE,{"disambiguationData":[TD([[makeQuery(id+"F0.imprint","IMPRINT",EDGE,{"derivedFrom":subQ0}),1.0]])]});}
            var Q28;
            {var subQ0=sQuery(id+"F0.wireOp",EDGE,"E11.17.1");Q28=makeQuery(id+"F0.imprint","IMPRINT",FACE,{"disambiguationData":[TD([[makeQuery(id+"F0.imprint","IMPRINT",EDGE,{"derivedFrom":subQ0}),-1.0]])]});}
            var Q29;
            {var subQ0=sQuery(id+"F0.wireOp",EDGE,"E11.16.1");Q29=makeQuery(id+"F0.imprint","IMPRINT",FACE,{"disambiguationData":[TD([[makeQuery(id+"F0.imprint","IMPRINT",EDGE,{"derivedFrom":subQ0}),1.0]])]});}
            var Q30;
            {var subQ0=sQuery(id+"F0.wireOp",EDGE,"E11.16.1");Q30=makeQuery(id+"F0.imprint","IMPRINT",FACE,{"disambiguationData":[TD([[makeQuery(id+"F0.imprint","IMPRINT",EDGE,{"derivedFrom":subQ0}),-1.0]])]});}
            var Q31;
            {var subQ0=sQuery(id+"F0.wireOp",EDGE,"E11.15.1");Q31=makeQuery(id+"F0.imprint","IMPRINT",FACE,{"disambiguationData":[TD([[makeQuery(id+"F0.imprint","IMPRINT",EDGE,{"derivedFrom":subQ0}),-1.0]])]});}
            var Q32;
            {var subQ0=sQuery(id+"F0.wireOp",EDGE,"E11.15.1");Q32=makeQuery(id+"F0.imprint","IMPRINT",FACE,{"disambiguationData":[TD([[makeQuery(id+"F0.imprint","IMPRINT",EDGE,{"derivedFrom":subQ0}),1.0]])]});}
            var Q33;
            {var subQ0=sQuery(id+"F0.wireOp",EDGE,"E11.14.1");Q33=makeQuery(id+"F0.imprint","IMPRINT",FACE,{"disambiguationData":[TD([[makeQuery(id+"F0.imprint","IMPRINT",EDGE,{"derivedFrom":subQ0}),1.0]])]});}
            var Q34;
            {var subQ0=sQuery(id+"F0.wireOp",EDGE,"E11.14.1");Q34=makeQuery(id+"F0.imprint","IMPRINT",FACE,{"disambiguationData":[TD([[makeQuery(id+"F0.imprint","IMPRINT",EDGE,{"derivedFrom":subQ0}),-1.0]])]});}
            var Q35;
            {var subQ0=sQuery(id+"F0.wireOp",EDGE,"E11.13.1");Q35=makeQuery(id+"F0.imprint","IMPRINT",FACE,{"disambiguationData":[TD([[makeQuery(id+"F0.imprint","IMPRINT",EDGE,{"derivedFrom":subQ0}),-1.0]])]});}
            var Q36;
            {var subQ0=sQuery(id+"F0.wireOp",EDGE,"E11.13.1");Q36=makeQuery(id+"F0.imprint","IMPRINT",FACE,{"disambiguationData":[TD([[makeQuery(id+"F0.imprint","IMPRINT",EDGE,{"derivedFrom":subQ0}),1.0]])]});}
            var Q37;
            {var subQ0=sQuery(id+"F0.wireOp",EDGE,"E11.12.1");Q37=makeQuery(id+"F0.imprint","IMPRINT",FACE,{"disambiguationData":[TD([[makeQuery(id+"F0.imprint","IMPRINT",EDGE,{"derivedFrom":subQ0}),-1.0]])]});}
            var Q38;
            {var subQ0=sQuery(id+"F0.wireOp",EDGE,"E11.12.1");Q38=makeQuery(id+"F0.imprint","IMPRINT",FACE,{"disambiguationData":[TD([[makeQuery(id+"F0.imprint","IMPRINT",EDGE,{"derivedFrom":subQ0}),1.0]])]});}
            var Q39;
            {var subQ0=sQuery(id+"F0.wireOp",EDGE,"E11.11.1");Q39=makeQuery(id+"F0.imprint","IMPRINT",FACE,{"disambiguationData":[TD([[makeQuery(id+"F0.imprint","IMPRINT",EDGE,{"derivedFrom":subQ0}),-1.0]])]});}
            var Q40;
            {var subQ0=sQuery(id+"F0.wireOp",EDGE,"E11.11.1");Q40=makeQuery(id+"F0.imprint","IMPRINT",FACE,{"disambiguationData":[TD([[makeQuery(id+"F0.imprint","IMPRINT",EDGE,{"derivedFrom":subQ0}),1.0]])]});}
            var Q41;
            {var subQ0=sQuery(id+"F0.wireOp",EDGE,"E11.10.1");Q41=makeQuery(id+"F0.imprint","IMPRINT",FACE,{"disambiguationData":[TD([[makeQuery(id+"F0.imprint","IMPRINT",EDGE,{"derivedFrom":subQ0}),-1.0]])]});}
            var Q42;
            {var subQ0=sQuery(id+"F0.wireOp",EDGE,"E11.10.1");Q42=makeQuery(id+"F0.imprint","IMPRINT",FACE,{"disambiguationData":[TD([[makeQuery(id+"F0.imprint","IMPRINT",EDGE,{"derivedFrom":subQ0}),1.0]])]});}
            var Q43;
            {var subQ0=sQuery(id+"F0.wireOp",EDGE,"E11.9.1");Q43=makeQuery(id+"F0.imprint","IMPRINT",FACE,{"disambiguationData":[TD([[makeQuery(id+"F0.imprint","IMPRINT",EDGE,{"derivedFrom":subQ0}),-1.0]])]});}
            var Q44;
            {var subQ0=sQuery(id+"F0.wireOp",EDGE,"E11.9.1");Q44=makeQuery(id+"F0.imprint","IMPRINT",FACE,{"disambiguationData":[TD([[makeQuery(id+"F0.imprint","IMPRINT",EDGE,{"derivedFrom":subQ0}),1.0]])]});}
            var Q45;
            {var subQ0=sQuery(id+"F0.wireOp",EDGE,"E11.8.1");Q45=makeQuery(id+"F0.imprint","IMPRINT",FACE,{"disambiguationData":[TD([[makeQuery(id+"F0.imprint","IMPRINT",EDGE,{"derivedFrom":subQ0}),-1.0]])]});}
            var Q46;
            {var subQ0=sQuery(id+"F0.wireOp",EDGE,"E11.8.1");Q46=makeQuery(id+"F0.imprint","IMPRINT",FACE,{"disambiguationData":[TD([[makeQuery(id+"F0.imprint","IMPRINT",EDGE,{"derivedFrom":subQ0}),1.0]])]});}
            var Q47;
            {var subQ0=sQuery(id+"F0.wireOp",EDGE,"E11.7.1");Q47=makeQuery(id+"F0.imprint","IMPRINT",FACE,{"disambiguationData":[TD([[makeQuery(id+"F0.imprint","IMPRINT",EDGE,{"derivedFrom":subQ0}),-1.0]])]});}
            var Q48;
            {var subQ0=sQuery(id+"F0.wireOp",EDGE,"E11.7.1");Q48=makeQuery(id+"F0.imprint","IMPRINT",FACE,{"disambiguationData":[TD([[makeQuery(id+"F0.imprint","IMPRINT",EDGE,{"derivedFrom":subQ0}),1.0]])]});}
            var Q49;
            {var subQ0=sQuery(id+"F0.wireOp",EDGE,"E11.6.1");Q49=makeQuery(id+"F0.imprint","IMPRINT",FACE,{"disambiguationData":[TD([[makeQuery(id+"F0.imprint","IMPRINT",EDGE,{"derivedFrom":subQ0}),1.0]])]});}
            var Q50;
            {var subQ0=sQuery(id+"F0.wireOp",EDGE,"E11.6.1");Q50=makeQuery(id+"F0.imprint","IMPRINT",FACE,{"disambiguationData":[TD([[makeQuery(id+"F0.imprint","IMPRINT",EDGE,{"derivedFrom":subQ0}),-1.0]])]});}
            var Q51;
            {var subQ0=sQuery(id+"F0.wireOp",EDGE,"E11.5.1");Q51=makeQuery(id+"F0.imprint","IMPRINT",FACE,{"disambiguationData":[TD([[makeQuery(id+"F0.imprint","IMPRINT",EDGE,{"derivedFrom":subQ0}),-1.0]])]});}
            var Q52;
            {var subQ0=sQuery(id+"F0.wireOp",EDGE,"E11.5.1");Q52=makeQuery(id+"F0.imprint","IMPRINT",FACE,{"disambiguationData":[TD([[makeQuery(id+"F0.imprint","IMPRINT",EDGE,{"derivedFrom":subQ0}),1.0]])]});}
            var Q53;
            {var subQ0=sQuery(id+"F0.wireOp",EDGE,"E11.4.1");Q53=makeQuery(id+"F0.imprint","IMPRINT",FACE,{"disambiguationData":[TD([[makeQuery(id+"F0.imprint","IMPRINT",EDGE,{"derivedFrom":subQ0}),1.0]])]});}
            var Q54;
            {var subQ0=sQuery(id+"F0.wireOp",EDGE,"E11.4.1");Q54=makeQuery(id+"F0.imprint","IMPRINT",FACE,{"disambiguationData":[TD([[makeQuery(id+"F0.imprint","IMPRINT",EDGE,{"derivedFrom":subQ0}),-1.0]])]});}
            var Q55;
            {var subQ0=sQuery(id+"F0.wireOp",EDGE,"E11.3.1");Q55=makeQuery(id+"F0.imprint","IMPRINT",FACE,{"disambiguationData":[TD([[makeQuery(id+"F0.imprint","IMPRINT",EDGE,{"derivedFrom":subQ0}),-1.0]])]});}
            var Q56;
            {var subQ0=sQuery(id+"F0.wireOp",EDGE,"E11.3.1");Q56=makeQuery(id+"F0.imprint","IMPRINT",FACE,{"disambiguationData":[TD([[makeQuery(id+"F0.imprint","IMPRINT",EDGE,{"derivedFrom":subQ0}),1.0]])]});}
            var Q57;
            {var subQ0=sQuery(id+"F0.wireOp",EDGE,"E11.2.1");Q57=makeQuery(id+"F0.imprint","IMPRINT",FACE,{"disambiguationData":[TD([[makeQuery(id+"F0.imprint","IMPRINT",EDGE,{"derivedFrom":subQ0}),1.0]])]});}
            var Q58;
            {var subQ0=sQuery(id+"F0.wireOp",EDGE,"E11.2.1");Q58=makeQuery(id+"F0.imprint","IMPRINT",FACE,{"disambiguationData":[TD([[makeQuery(id+"F0.imprint","IMPRINT",EDGE,{"derivedFrom":subQ0}),-1.0]])]});}
            var Q59;
            {var subQ0=sQuery(id+"F0.wireOp",EDGE,"E11.1.1");Q59=makeQuery(id+"F0.imprint","IMPRINT",FACE,{"disambiguationData":[TD([[makeQuery(id+"F0.imprint","IMPRINT",EDGE,{"derivedFrom":subQ0}),-1.0]])]});}
            var Q60;
            {var subQ0=sQuery(id+"F0.wireOp",EDGE,"E11.1.1");Q60=makeQuery(id+"F0.imprint","IMPRINT",FACE,{"disambiguationData":[TD([[makeQuery(id+"F0.imprint","IMPRINT",EDGE,{"derivedFrom":subQ0}),1.0]])]});}
            extrude(context, id + "F1", {"entities" : qUnion([Q0, Q1, Q2, Q3, Q4, Q5, Q6, Q7, Q8, Q9, Q10, Q11, Q12, Q13, Q14, Q15, Q16, Q17, Q18, Q19, Q20, Q21, Q22, Q23, Q24, Q25, Q26, Q27, Q28, Q29, Q30, Q31, Q32, Q33, Q34, Q35, Q36, Q37, Q38, Q39, Q40, Q41, Q42, Q43, Q44, Q45, Q46, Q47, Q48, Q49, Q50, Q51, Q52, Q53, Q54, Q55, Q56, Q57, Q58, Q59, Q60]), "depth" : 170 * mm, "offsetDistance" : 25 * mm});
        }
        {
            var Q0;
            Q0=qCreatedBy(makeId("Front.planeOp"),FACE);
            cPlane(context, id + "F2", {"entities" : qUnion([Q0]), "cplaneType" : CPlaneType.OFFSET, "offset" : 170 * mm, "width" : 150 * mm, "height" : 150 * mm});
        }
        {
            var Q0;
            Q0=qCreatedBy(id+"F2.planeOp",FACE);
            var sketch = newSketch(context, id + "F3", { "sketchPlane" : qUnion([Q0])});
            skCircle(sketch, "E17", {"center": v(0, 0) * mm, "radius": 3680 * mm});
            skPoint(sketch, "E18", {"position": v(-3700, 0) * mm});
            skPoint(sketch, "E19", {"position": v(-3680, 0) * mm});
            skLineSegment(sketch, "E20", {"start": v(-3680, 0) * mm, "end": v(0, 0) * mm, "construction": true});
            skPoint(sketch, "E21", {"position": v(-3530, 0) * mm});
            skLineSegment(sketch, "E22", {"start": v(-3680, 0) * mm, "end": v(-3530, 0) * mm});
            skPoint(sketch, "E23", {"position": v(-3680, 2) * mm});
            skPoint(sketch, "E24", {"position": v(-3680, -2) * mm});
            skLineSegment(sketch, "E25", {"start": v(-3680, 2) * mm, "end": v(-3530, 2) * mm});
            skLineSegment(sketch, "E26", {"start": v(-3680, -2) * mm, "end": v(-3530, -2) * mm});
            skLineSegment(sketch, "E27", {"start": v(-3530, -2) * mm, "end": v(-3530, 2) * mm});
            skPoint(sketch, "E28.1.0", {"position": v(-3599.17, -767.07) * mm});
            skLineSegment(sketch, "E28.1.1", {"start": v(-3599.58, -765.12) * mm, "end": v(-3452.86, -733.93) * mm});
            skLineSegment(sketch, "E28.1.2", {"start": v(-3599.17, -767.07) * mm, "end": v(-3452.45, -735.88) * mm});
            skLineSegment(sketch, "E28.1.3", {"start": v(-3600, -763.16) * mm, "end": v(-3453.28, -731.97) * mm});
            skPoint(sketch, "E28.1.4", {"position": v(-3600, -763.16) * mm});
            skPoint(sketch, "E28.1.5", {"position": v(-3452.86, -733.93) * mm});
            skPoint(sketch, "E28.1.6", {"position": v(-3599.58, -765.12) * mm});
            skLineSegment(sketch, "E28.1.7", {"start": v(-3452.45, -735.88) * mm, "end": v(-3453.28, -731.97) * mm});
            skPoint(sketch, "E28.2.0", {"position": v(-3361.03, -1498.62) * mm});
            skLineSegment(sketch, "E28.2.1", {"start": v(-3361.85, -1496.8) * mm, "end": v(-3224.82, -1435.78) * mm});
            skLineSegment(sketch, "E28.2.2", {"start": v(-3361.03, -1498.62) * mm, "end": v(-3224, -1437.6) * mm});
            skLineSegment(sketch, "E28.2.3", {"start": v(-3362.66, -1494.96) * mm, "end": v(-3225.63, -1433.95) * mm});
            skPoint(sketch, "E28.2.4", {"position": v(-3362.66, -1494.96) * mm});
            skPoint(sketch, "E28.2.5", {"position": v(-3224.82, -1435.78) * mm});
            skPoint(sketch, "E28.2.6", {"position": v(-3361.85, -1496.8) * mm});
            skLineSegment(sketch, "E28.2.7", {"start": v(-3224, -1437.6) * mm, "end": v(-3225.63, -1433.95) * mm});
            skPoint(sketch, "E28.3.0", {"position": v(-2976, -2164.67) * mm});
            skLineSegment(sketch, "E28.3.1", {"start": v(-2977.18, -2163.05) * mm, "end": v(-2855.83, -2074.88) * mm});
            skLineSegment(sketch, "E28.3.2", {"start": v(-2976, -2164.67) * mm, "end": v(-2854.65, -2076.5) * mm});
            skLineSegment(sketch, "E28.3.3", {"start": v(-2978.36, -2161.43) * mm, "end": v(-2857, -2073.26) * mm});
            skPoint(sketch, "E28.3.4", {"position": v(-2978.36, -2161.43) * mm});
            skPoint(sketch, "E28.3.5", {"position": v(-2855.83, -2074.88) * mm});
            skPoint(sketch, "E28.3.6", {"position": v(-2977.18, -2163.05) * mm});
            skLineSegment(sketch, "E28.3.7", {"start": v(-2854.65, -2076.5) * mm, "end": v(-2857, -2073.26) * mm});
            skPoint(sketch, "E28.4.0", {"position": v(-2460.91, -2736.11) * mm});
            skLineSegment(sketch, "E28.4.1", {"start": v(-2462.4, -2734.77) * mm, "end": v(-2362.03, -2623.3) * mm});
            skLineSegment(sketch, "E28.4.2", {"start": v(-2460.91, -2736.11) * mm, "end": v(-2360.54, -2624.64) * mm});
            skLineSegment(sketch, "E28.4.3", {"start": v(-2463.89, -2733.43) * mm, "end": v(-2363.52, -2621.96) * mm});
            skPoint(sketch, "E28.4.4", {"position": v(-2463.89, -2733.43) * mm});
            skPoint(sketch, "E28.4.5", {"position": v(-2362.03, -2623.3) * mm});
            skPoint(sketch, "E28.4.6", {"position": v(-2462.4, -2734.77) * mm});
            skLineSegment(sketch, "E28.4.7", {"start": v(-2360.54, -2624.64) * mm, "end": v(-2363.52, -2621.96) * mm});
            skPoint(sketch, "E28.5.0", {"position": v(-1838.27, -3187.97) * mm});
            skLineSegment(sketch, "E28.5.1", {"start": v(-1840, -3186.97) * mm, "end": v(-1765, -3057.07) * mm});
            skLineSegment(sketch, "E28.5.2", {"start": v(-1838.27, -3187.97) * mm, "end": v(-1763.27, -3058.07) * mm});
            skLineSegment(sketch, "E28.5.3", {"start": v(-1841.73, -3185.97) * mm, "end": v(-1766.73, -3056.07) * mm});
            skPoint(sketch, "E28.5.4", {"position": v(-1841.73, -3185.97) * mm});
            skPoint(sketch, "E28.5.5", {"position": v(-1765, -3057.07) * mm});
            skPoint(sketch, "E28.5.6", {"position": v(-1840, -3186.97) * mm});
            skLineSegment(sketch, "E28.5.7", {"start": v(-1763.27, -3058.07) * mm, "end": v(-1766.73, -3056.07) * mm});
            skPoint(sketch, "E28.6.0", {"position": v(-1135.28, -3500.5) * mm});
            skLineSegment(sketch, "E28.6.1", {"start": v(-1137.18, -3499.89) * mm, "end": v(-1090.83, -3357.23) * mm});
            skLineSegment(sketch, "E28.6.2", {"start": v(-1135.28, -3500.5) * mm, "end": v(-1088.93, -3357.85) * mm});
            skLineSegment(sketch, "E28.6.3", {"start": v(-1139.08, -3499.27) * mm, "end": v(-1092.73, -3356.61) * mm});
            skPoint(sketch, "E28.6.4", {"position": v(-1139.08, -3499.27) * mm});
            skPoint(sketch, "E28.6.5", {"position": v(-1090.83, -3357.23) * mm});
            skPoint(sketch, "E28.6.6", {"position": v(-1137.18, -3499.89) * mm});
            skLineSegment(sketch, "E28.6.7", {"start": v(-1088.93, -3357.85) * mm, "end": v(-1092.73, -3356.61) * mm});
            skPoint(sketch, "E28.7.0", {"position": v(-382.68, -3660.05) * mm});
            skLineSegment(sketch, "E28.7.1", {"start": v(-384.66, -3659.84) * mm, "end": v(-368.99, -3510.66) * mm});
            skLineSegment(sketch, "E28.7.2", {"start": v(-382.68, -3660.05) * mm, "end": v(-367, -3510.87) * mm});
            skLineSegment(sketch, "E28.7.3", {"start": v(-386.65, -3659.63) * mm, "end": v(-370.97, -3510.45) * mm});
            skPoint(sketch, "E28.7.4", {"position": v(-386.65, -3659.63) * mm});
            skPoint(sketch, "E28.7.5", {"position": v(-368.99, -3510.66) * mm});
            skPoint(sketch, "E28.7.6", {"position": v(-384.66, -3659.84) * mm});
            skLineSegment(sketch, "E28.7.7", {"start": v(-367, -3510.87) * mm, "end": v(-370.97, -3510.45) * mm});
            skPoint(sketch, "E28.8.0", {"position": v(386.65, -3659.63) * mm});
            skLineSegment(sketch, "E28.8.1", {"start": v(384.66, -3659.84) * mm, "end": v(368.99, -3510.66) * mm});
            skLineSegment(sketch, "E28.8.2", {"start": v(386.65, -3659.63) * mm, "end": v(370.97, -3510.45) * mm});
            skLineSegment(sketch, "E28.8.3", {"start": v(382.68, -3660.05) * mm, "end": v(367, -3510.87) * mm});
            skPoint(sketch, "E28.8.4", {"position": v(382.68, -3660.05) * mm});
            skPoint(sketch, "E28.8.5", {"position": v(368.99, -3510.66) * mm});
            skPoint(sketch, "E28.8.6", {"position": v(384.66, -3659.84) * mm});
            skLineSegment(sketch, "E28.8.7", {"start": v(370.97, -3510.45) * mm, "end": v(367, -3510.87) * mm});
            skPoint(sketch, "E28.9.0", {"position": v(1139.08, -3499.27) * mm});
            skLineSegment(sketch, "E28.9.1", {"start": v(1137.18, -3499.89) * mm, "end": v(1090.83, -3357.23) * mm});
            skLineSegment(sketch, "E28.9.2", {"start": v(1139.08, -3499.27) * mm, "end": v(1092.73, -3356.61) * mm});
            skLineSegment(sketch, "E28.9.3", {"start": v(1135.28, -3500.5) * mm, "end": v(1088.93, -3357.85) * mm});
            skPoint(sketch, "E28.9.4", {"position": v(1135.28, -3500.5) * mm});
            skPoint(sketch, "E28.9.5", {"position": v(1090.83, -3357.23) * mm});
            skPoint(sketch, "E28.9.6", {"position": v(1137.18, -3499.89) * mm});
            skLineSegment(sketch, "E28.9.7", {"start": v(1092.73, -3356.61) * mm, "end": v(1088.93, -3357.85) * mm});
            skPoint(sketch, "E28.10.0", {"position": v(1841.73, -3185.97) * mm});
            skLineSegment(sketch, "E28.10.1", {"start": v(1840, -3186.97) * mm, "end": v(1765, -3057.07) * mm});
            skLineSegment(sketch, "E28.10.2", {"start": v(1841.73, -3185.97) * mm, "end": v(1766.73, -3056.07) * mm});
            skLineSegment(sketch, "E28.10.3", {"start": v(1838.27, -3187.97) * mm, "end": v(1763.27, -3058.07) * mm});
            skPoint(sketch, "E28.10.4", {"position": v(1838.27, -3187.97) * mm});
            skPoint(sketch, "E28.10.5", {"position": v(1765, -3057.07) * mm});
            skPoint(sketch, "E28.10.6", {"position": v(1840, -3186.97) * mm});
            skLineSegment(sketch, "E28.10.7", {"start": v(1766.73, -3056.07) * mm, "end": v(1763.27, -3058.07) * mm});
            skPoint(sketch, "E28.11.0", {"position": v(2463.89, -2733.43) * mm});
            skLineSegment(sketch, "E28.11.1", {"start": v(2462.4, -2734.77) * mm, "end": v(2362.03, -2623.3) * mm});
            skLineSegment(sketch, "E28.11.2", {"start": v(2463.89, -2733.43) * mm, "end": v(2363.52, -2621.96) * mm});
            skLineSegment(sketch, "E28.11.3", {"start": v(2460.91, -2736.11) * mm, "end": v(2360.54, -2624.64) * mm});
            skPoint(sketch, "E28.11.4", {"position": v(2460.91, -2736.11) * mm});
            skPoint(sketch, "E28.11.5", {"position": v(2362.03, -2623.3) * mm});
            skPoint(sketch, "E28.11.6", {"position": v(2462.4, -2734.77) * mm});
            skLineSegment(sketch, "E28.11.7", {"start": v(2363.52, -2621.96) * mm, "end": v(2360.54, -2624.64) * mm});
            skPoint(sketch, "E28.12.0", {"position": v(2978.36, -2161.43) * mm});
            skLineSegment(sketch, "E28.12.1", {"start": v(2977.18, -2163.05) * mm, "end": v(2855.83, -2074.88) * mm});
            skLineSegment(sketch, "E28.12.2", {"start": v(2978.36, -2161.43) * mm, "end": v(2857, -2073.26) * mm});
            skLineSegment(sketch, "E28.12.3", {"start": v(2976, -2164.67) * mm, "end": v(2854.65, -2076.5) * mm});
            skPoint(sketch, "E28.12.4", {"position": v(2976, -2164.67) * mm});
            skPoint(sketch, "E28.12.5", {"position": v(2855.83, -2074.88) * mm});
            skPoint(sketch, "E28.12.6", {"position": v(2977.18, -2163.05) * mm});
            skLineSegment(sketch, "E28.12.7", {"start": v(2857, -2073.26) * mm, "end": v(2854.65, -2076.5) * mm});
            skPoint(sketch, "E28.13.0", {"position": v(3362.66, -1494.96) * mm});
            skLineSegment(sketch, "E28.13.1", {"start": v(3361.85, -1496.8) * mm, "end": v(3224.82, -1435.78) * mm});
            skLineSegment(sketch, "E28.13.2", {"start": v(3362.66, -1494.96) * mm, "end": v(3225.63, -1433.95) * mm});
            skLineSegment(sketch, "E28.13.3", {"start": v(3361.03, -1498.62) * mm, "end": v(3224, -1437.6) * mm});
            skPoint(sketch, "E28.13.4", {"position": v(3361.03, -1498.62) * mm});
            skPoint(sketch, "E28.13.5", {"position": v(3224.82, -1435.78) * mm});
            skPoint(sketch, "E28.13.6", {"position": v(3361.85, -1496.8) * mm});
            skLineSegment(sketch, "E28.13.7", {"start": v(3225.63, -1433.95) * mm, "end": v(3224, -1437.6) * mm});
            skPoint(sketch, "E28.14.0", {"position": v(3600, -763.16) * mm});
            skLineSegment(sketch, "E28.14.1", {"start": v(3599.58, -765.12) * mm, "end": v(3452.86, -733.93) * mm});
            skLineSegment(sketch, "E28.14.2", {"start": v(3600, -763.16) * mm, "end": v(3453.28, -731.97) * mm});
            skLineSegment(sketch, "E28.14.3", {"start": v(3599.17, -767.07) * mm, "end": v(3452.45, -735.88) * mm});
            skPoint(sketch, "E28.14.4", {"position": v(3599.17, -767.07) * mm});
            skPoint(sketch, "E28.14.5", {"position": v(3452.86, -733.93) * mm});
            skPoint(sketch, "E28.14.6", {"position": v(3599.58, -765.12) * mm});
            skLineSegment(sketch, "E28.14.7", {"start": v(3453.28, -731.97) * mm, "end": v(3452.45, -735.88) * mm});
            skPoint(sketch, "E28.15.0", {"position": v(3680, 2) * mm});
            skLineSegment(sketch, "E28.15.1", {"start": v(3680, 0) * mm, "end": v(3530, 0) * mm});
            skLineSegment(sketch, "E28.15.2", {"start": v(3680, 2) * mm, "end": v(3530, 2) * mm});
            skLineSegment(sketch, "E28.15.3", {"start": v(3680, -2) * mm, "end": v(3530, -2) * mm});
            skPoint(sketch, "E28.15.4", {"position": v(3680, -2) * mm});
            skPoint(sketch, "E28.15.5", {"position": v(3530, 0) * mm});
            skPoint(sketch, "E28.15.6", {"position": v(3680, 0) * mm});
            skLineSegment(sketch, "E28.15.7", {"start": v(3530, 2) * mm, "end": v(3530, -2) * mm});
            skPoint(sketch, "E28.16.0", {"position": v(3599.17, 767.07) * mm});
            skLineSegment(sketch, "E28.16.1", {"start": v(3599.58, 765.12) * mm, "end": v(3452.86, 733.93) * mm});
            skLineSegment(sketch, "E28.16.2", {"start": v(3599.17, 767.07) * mm, "end": v(3452.45, 735.88) * mm});
            skLineSegment(sketch, "E28.16.3", {"start": v(3600, 763.16) * mm, "end": v(3453.28, 731.97) * mm});
            skPoint(sketch, "E28.16.4", {"position": v(3600, 763.16) * mm});
            skPoint(sketch, "E28.16.5", {"position": v(3452.86, 733.93) * mm});
            skPoint(sketch, "E28.16.6", {"position": v(3599.58, 765.12) * mm});
            skLineSegment(sketch, "E28.16.7", {"start": v(3452.45, 735.88) * mm, "end": v(3453.28, 731.97) * mm});
            skPoint(sketch, "E28.17.0", {"position": v(3361.03, 1498.62) * mm});
            skLineSegment(sketch, "E28.17.1", {"start": v(3361.85, 1496.8) * mm, "end": v(3224.82, 1435.78) * mm});
            skLineSegment(sketch, "E28.17.2", {"start": v(3361.03, 1498.62) * mm, "end": v(3224, 1437.6) * mm});
            skLineSegment(sketch, "E28.17.3", {"start": v(3362.66, 1494.96) * mm, "end": v(3225.63, 1433.95) * mm});
            skPoint(sketch, "E28.17.4", {"position": v(3362.66, 1494.96) * mm});
            skPoint(sketch, "E28.17.5", {"position": v(3224.82, 1435.78) * mm});
            skPoint(sketch, "E28.17.6", {"position": v(3361.85, 1496.8) * mm});
            skLineSegment(sketch, "E28.17.7", {"start": v(3224, 1437.6) * mm, "end": v(3225.63, 1433.95) * mm});
            skPoint(sketch, "E28.18.0", {"position": v(2976, 2164.67) * mm});
            skLineSegment(sketch, "E28.18.1", {"start": v(2977.18, 2163.05) * mm, "end": v(2855.83, 2074.88) * mm});
            skLineSegment(sketch, "E28.18.2", {"start": v(2976, 2164.67) * mm, "end": v(2854.65, 2076.5) * mm});
            skLineSegment(sketch, "E28.18.3", {"start": v(2978.36, 2161.43) * mm, "end": v(2857, 2073.26) * mm});
            skPoint(sketch, "E28.18.4", {"position": v(2978.36, 2161.43) * mm});
            skPoint(sketch, "E28.18.5", {"position": v(2855.83, 2074.88) * mm});
            skPoint(sketch, "E28.18.6", {"position": v(2977.18, 2163.05) * mm});
            skLineSegment(sketch, "E28.18.7", {"start": v(2854.65, 2076.5) * mm, "end": v(2857, 2073.26) * mm});
            skPoint(sketch, "E28.19.0", {"position": v(2460.91, 2736.11) * mm});
            skLineSegment(sketch, "E28.19.1", {"start": v(2462.4, 2734.77) * mm, "end": v(2362.03, 2623.3) * mm});
            skLineSegment(sketch, "E28.19.2", {"start": v(2460.91, 2736.11) * mm, "end": v(2360.54, 2624.64) * mm});
            skLineSegment(sketch, "E28.19.3", {"start": v(2463.89, 2733.43) * mm, "end": v(2363.52, 2621.96) * mm});
            skPoint(sketch, "E28.19.4", {"position": v(2463.89, 2733.43) * mm});
            skPoint(sketch, "E28.19.5", {"position": v(2362.03, 2623.3) * mm});
            skPoint(sketch, "E28.19.6", {"position": v(2462.4, 2734.77) * mm});
            skLineSegment(sketch, "E28.19.7", {"start": v(2360.54, 2624.64) * mm, "end": v(2363.52, 2621.96) * mm});
            skPoint(sketch, "E28.20.0", {"position": v(1838.27, 3187.97) * mm});
            skLineSegment(sketch, "E28.20.1", {"start": v(1840, 3186.97) * mm, "end": v(1765, 3057.07) * mm});
            skLineSegment(sketch, "E28.20.2", {"start": v(1838.27, 3187.97) * mm, "end": v(1763.27, 3058.07) * mm});
            skLineSegment(sketch, "E28.20.3", {"start": v(1841.73, 3185.97) * mm, "end": v(1766.73, 3056.07) * mm});
            skPoint(sketch, "E28.20.4", {"position": v(1841.73, 3185.97) * mm});
            skPoint(sketch, "E28.20.5", {"position": v(1765, 3057.07) * mm});
            skPoint(sketch, "E28.20.6", {"position": v(1840, 3186.97) * mm});
            skLineSegment(sketch, "E28.20.7", {"start": v(1763.27, 3058.07) * mm, "end": v(1766.73, 3056.07) * mm});
            skPoint(sketch, "E28.21.0", {"position": v(1135.28, 3500.5) * mm});
            skLineSegment(sketch, "E28.21.1", {"start": v(1137.18, 3499.89) * mm, "end": v(1090.83, 3357.23) * mm});
            skLineSegment(sketch, "E28.21.2", {"start": v(1135.28, 3500.5) * mm, "end": v(1088.93, 3357.85) * mm});
            skLineSegment(sketch, "E28.21.3", {"start": v(1139.08, 3499.27) * mm, "end": v(1092.73, 3356.61) * mm});
            skPoint(sketch, "E28.21.4", {"position": v(1139.08, 3499.27) * mm});
            skPoint(sketch, "E28.21.5", {"position": v(1090.83, 3357.23) * mm});
            skPoint(sketch, "E28.21.6", {"position": v(1137.18, 3499.89) * mm});
            skLineSegment(sketch, "E28.21.7", {"start": v(1088.93, 3357.85) * mm, "end": v(1092.73, 3356.61) * mm});
            skPoint(sketch, "E28.22.0", {"position": v(382.68, 3660.05) * mm});
            skLineSegment(sketch, "E28.22.1", {"start": v(384.66, 3659.84) * mm, "end": v(368.99, 3510.66) * mm});
            skLineSegment(sketch, "E28.22.2", {"start": v(382.68, 3660.05) * mm, "end": v(367, 3510.87) * mm});
            skLineSegment(sketch, "E28.22.3", {"start": v(386.65, 3659.63) * mm, "end": v(370.97, 3510.45) * mm});
            skPoint(sketch, "E28.22.4", {"position": v(386.65, 3659.63) * mm});
            skPoint(sketch, "E28.22.5", {"position": v(368.99, 3510.66) * mm});
            skPoint(sketch, "E28.22.6", {"position": v(384.66, 3659.84) * mm});
            skLineSegment(sketch, "E28.22.7", {"start": v(367, 3510.87) * mm, "end": v(370.97, 3510.45) * mm});
            skPoint(sketch, "E28.23.0", {"position": v(-386.65, 3659.63) * mm});
            skLineSegment(sketch, "E28.23.1", {"start": v(-384.66, 3659.84) * mm, "end": v(-368.99, 3510.66) * mm});
            skLineSegment(sketch, "E28.23.2", {"start": v(-386.65, 3659.63) * mm, "end": v(-370.97, 3510.45) * mm});
            skLineSegment(sketch, "E28.23.3", {"start": v(-382.68, 3660.05) * mm, "end": v(-367, 3510.87) * mm});
            skPoint(sketch, "E28.23.4", {"position": v(-382.68, 3660.05) * mm});
            skPoint(sketch, "E28.23.5", {"position": v(-368.99, 3510.66) * mm});
            skPoint(sketch, "E28.23.6", {"position": v(-384.66, 3659.84) * mm});
            skLineSegment(sketch, "E28.23.7", {"start": v(-370.97, 3510.45) * mm, "end": v(-367, 3510.87) * mm});
            skPoint(sketch, "E28.24.0", {"position": v(-1139.08, 3499.27) * mm});
            skLineSegment(sketch, "E28.24.1", {"start": v(-1137.18, 3499.89) * mm, "end": v(-1090.83, 3357.23) * mm});
            skLineSegment(sketch, "E28.24.2", {"start": v(-1139.08, 3499.27) * mm, "end": v(-1092.73, 3356.61) * mm});
            skLineSegment(sketch, "E28.24.3", {"start": v(-1135.28, 3500.5) * mm, "end": v(-1088.93, 3357.85) * mm});
            skPoint(sketch, "E28.24.4", {"position": v(-1135.28, 3500.5) * mm});
            skPoint(sketch, "E28.24.5", {"position": v(-1090.83, 3357.23) * mm});
            skPoint(sketch, "E28.24.6", {"position": v(-1137.18, 3499.89) * mm});
            skLineSegment(sketch, "E28.24.7", {"start": v(-1092.73, 3356.61) * mm, "end": v(-1088.93, 3357.85) * mm});
            skPoint(sketch, "E28.25.0", {"position": v(-1841.73, 3185.97) * mm});
            skLineSegment(sketch, "E28.25.1", {"start": v(-1840, 3186.97) * mm, "end": v(-1765, 3057.07) * mm});
            skLineSegment(sketch, "E28.25.2", {"start": v(-1841.73, 3185.97) * mm, "end": v(-1766.73, 3056.07) * mm});
            skLineSegment(sketch, "E28.25.3", {"start": v(-1838.27, 3187.97) * mm, "end": v(-1763.27, 3058.07) * mm});
            skPoint(sketch, "E28.25.4", {"position": v(-1838.27, 3187.97) * mm});
            skPoint(sketch, "E28.25.5", {"position": v(-1765, 3057.07) * mm});
            skPoint(sketch, "E28.25.6", {"position": v(-1840, 3186.97) * mm});
            skLineSegment(sketch, "E28.25.7", {"start": v(-1766.73, 3056.07) * mm, "end": v(-1763.27, 3058.07) * mm});
            skPoint(sketch, "E28.26.0", {"position": v(-2463.89, 2733.43) * mm});
            skLineSegment(sketch, "E28.26.1", {"start": v(-2462.4, 2734.77) * mm, "end": v(-2362.03, 2623.3) * mm});
            skLineSegment(sketch, "E28.26.2", {"start": v(-2463.89, 2733.43) * mm, "end": v(-2363.52, 2621.96) * mm});
            skLineSegment(sketch, "E28.26.3", {"start": v(-2460.91, 2736.11) * mm, "end": v(-2360.54, 2624.64) * mm});
            skPoint(sketch, "E28.26.4", {"position": v(-2460.91, 2736.11) * mm});
            skPoint(sketch, "E28.26.5", {"position": v(-2362.03, 2623.3) * mm});
            skPoint(sketch, "E28.26.6", {"position": v(-2462.4, 2734.77) * mm});
            skLineSegment(sketch, "E28.26.7", {"start": v(-2363.52, 2621.96) * mm, "end": v(-2360.54, 2624.64) * mm});
            skPoint(sketch, "E28.27.0", {"position": v(-2978.36, 2161.43) * mm});
            skLineSegment(sketch, "E28.27.1", {"start": v(-2977.18, 2163.05) * mm, "end": v(-2855.83, 2074.88) * mm});
            skLineSegment(sketch, "E28.27.2", {"start": v(-2978.36, 2161.43) * mm, "end": v(-2857, 2073.26) * mm});
            skLineSegment(sketch, "E28.27.3", {"start": v(-2976, 2164.67) * mm, "end": v(-2854.65, 2076.5) * mm});
            skPoint(sketch, "E28.27.4", {"position": v(-2976, 2164.67) * mm});
            skPoint(sketch, "E28.27.5", {"position": v(-2855.83, 2074.88) * mm});
            skPoint(sketch, "E28.27.6", {"position": v(-2977.18, 2163.05) * mm});
            skLineSegment(sketch, "E28.27.7", {"start": v(-2857, 2073.26) * mm, "end": v(-2854.65, 2076.5) * mm});
            skPoint(sketch, "E28.28.0", {"position": v(-3362.66, 1494.96) * mm});
            skLineSegment(sketch, "E28.28.1", {"start": v(-3361.85, 1496.8) * mm, "end": v(-3224.82, 1435.78) * mm});
            skLineSegment(sketch, "E28.28.2", {"start": v(-3362.66, 1494.96) * mm, "end": v(-3225.63, 1433.95) * mm});
            skLineSegment(sketch, "E28.28.3", {"start": v(-3361.03, 1498.62) * mm, "end": v(-3224, 1437.6) * mm});
            skPoint(sketch, "E28.28.4", {"position": v(-3361.03, 1498.62) * mm});
            skPoint(sketch, "E28.28.5", {"position": v(-3224.82, 1435.78) * mm});
            skPoint(sketch, "E28.28.6", {"position": v(-3361.85, 1496.8) * mm});
            skLineSegment(sketch, "E28.28.7", {"start": v(-3225.63, 1433.95) * mm, "end": v(-3224, 1437.6) * mm});
            skPoint(sketch, "E28.29.0", {"position": v(-3600, 763.16) * mm});
            skLineSegment(sketch, "E28.29.1", {"start": v(-3599.58, 765.12) * mm, "end": v(-3452.86, 733.93) * mm});
            skLineSegment(sketch, "E28.29.2", {"start": v(-3600, 763.16) * mm, "end": v(-3453.28, 731.97) * mm});
            skLineSegment(sketch, "E28.29.3", {"start": v(-3599.17, 767.07) * mm, "end": v(-3452.45, 735.88) * mm});
            skPoint(sketch, "E28.29.4", {"position": v(-3599.17, 767.07) * mm});
            skPoint(sketch, "E28.29.5", {"position": v(-3452.86, 733.93) * mm});
            skPoint(sketch, "E28.29.6", {"position": v(-3599.58, 765.12) * mm});
            skLineSegment(sketch, "E28.29.7", {"start": v(-3453.28, 731.97) * mm, "end": v(-3452.45, 735.88) * mm});
            skLineSegment(sketch, "E29", {"start": v(-3453.28, 731.97) * mm, "end": v(-3530, 2) * mm});
            skLineSegment(sketch, "E30", {"start": v(-3452.86, 733.93) * mm, "end": v(-3445.57, 732.38) * mm, "construction": true});
            skPoint(sketch, "E31", {"position": v(-3526, 0) * mm});
            skLineSegment(sketch, "E32", {"start": v(-3526, 0) * mm, "end": v(-3448.95, 733.1) * mm});
            skLineSegment(sketch, "E33.1.0", {"start": v(-3530, -2) * mm, "end": v(-3453.28, -731.97) * mm});
            skLineSegment(sketch, "E33.1.1", {"start": v(-3448.95, -733.1) * mm, "end": v(-3526, 0) * mm});
            skLineSegment(sketch, "E33.1.2", {"start": v(-3530, 0) * mm, "end": v(-3522.54, 0) * mm, "construction": true});
            skLineSegment(sketch, "E33.2.0", {"start": v(-3452.45, -735.88) * mm, "end": v(-3225.63, -1433.95) * mm});
            skLineSegment(sketch, "E33.2.1", {"start": v(-3221.16, -1434.15) * mm, "end": v(-3448.95, -733.1) * mm});
            skLineSegment(sketch, "E33.2.2", {"start": v(-3452.86, -733.93) * mm, "end": v(-3445.57, -732.38) * mm, "construction": true});
            skLineSegment(sketch, "E33.3.0", {"start": v(-3224, -1437.6) * mm, "end": v(-2857, -2073.26) * mm});
            skLineSegment(sketch, "E33.3.1", {"start": v(-2852.6, -2072.53) * mm, "end": v(-3221.16, -1434.15) * mm});
            skLineSegment(sketch, "E33.3.2", {"start": v(-3224.82, -1435.78) * mm, "end": v(-3218, -1432.75) * mm, "construction": true});
            skLineSegment(sketch, "E33.4.0", {"start": v(-2854.65, -2076.5) * mm, "end": v(-2363.52, -2621.96) * mm});
            skLineSegment(sketch, "E33.4.1", {"start": v(-2359.35, -2620.33) * mm, "end": v(-2852.6, -2072.53) * mm});
            skLineSegment(sketch, "E33.4.2", {"start": v(-2855.83, -2074.88) * mm, "end": v(-2849.8, -2070.5) * mm, "construction": true});
            skLineSegment(sketch, "E33.5.0", {"start": v(-2360.54, -2624.64) * mm, "end": v(-1766.73, -3056.07) * mm});
            skLineSegment(sketch, "E33.5.1", {"start": v(-1763, -3053.6) * mm, "end": v(-2359.35, -2620.33) * mm});
            skLineSegment(sketch, "E33.5.2", {"start": v(-2362.03, -2623.3) * mm, "end": v(-2357.04, -2617.76) * mm, "construction": true});
            skLineSegment(sketch, "E33.6.0", {"start": v(-1763.27, -3058.07) * mm, "end": v(-1092.73, -3356.61) * mm});
            skLineSegment(sketch, "E33.6.1", {"start": v(-1089.6, -3353.43) * mm, "end": v(-1763, -3053.6) * mm});
            skLineSegment(sketch, "E33.6.2", {"start": v(-1765, -3057.07) * mm, "end": v(-1761.27, -3050.61) * mm, "construction": true});
            skLineSegment(sketch, "E33.7.0", {"start": v(-1088.93, -3357.85) * mm, "end": v(-370.97, -3510.45) * mm});
            skLineSegment(sketch, "E33.7.1", {"start": v(-368.57, -3506.68) * mm, "end": v(-1089.6, -3353.43) * mm});
            skLineSegment(sketch, "E33.7.2", {"start": v(-1090.83, -3357.23) * mm, "end": v(-1088.53, -3350.14) * mm, "construction": true});
            skLineSegment(sketch, "E33.8.0", {"start": v(-367, -3510.87) * mm, "end": v(367, -3510.87) * mm});
            skLineSegment(sketch, "E33.8.1", {"start": v(368.57, -3506.68) * mm, "end": v(-368.57, -3506.68) * mm});
            skLineSegment(sketch, "E33.8.2", {"start": v(-368.99, -3510.66) * mm, "end": v(-368.2, -3503.25) * mm, "construction": true});
            skLineSegment(sketch, "E33.9.0", {"start": v(370.97, -3510.45) * mm, "end": v(1088.93, -3357.85) * mm});
            skLineSegment(sketch, "E33.9.1", {"start": v(1089.6, -3353.43) * mm, "end": v(368.57, -3506.68) * mm});
            skLineSegment(sketch, "E33.9.2", {"start": v(368.99, -3510.66) * mm, "end": v(368.2, -3503.25) * mm, "construction": true});
            skLineSegment(sketch, "E33.10.0", {"start": v(1092.73, -3356.61) * mm, "end": v(1763.27, -3058.07) * mm});
            skLineSegment(sketch, "E33.10.1", {"start": v(1763, -3053.6) * mm, "end": v(1089.6, -3353.43) * mm});
            skLineSegment(sketch, "E33.10.2", {"start": v(1090.83, -3357.23) * mm, "end": v(1088.53, -3350.14) * mm, "construction": true});
            skLineSegment(sketch, "E33.11.0", {"start": v(1766.73, -3056.07) * mm, "end": v(2360.54, -2624.64) * mm});
            skLineSegment(sketch, "E33.11.1", {"start": v(2359.35, -2620.33) * mm, "end": v(1763, -3053.6) * mm});
            skLineSegment(sketch, "E33.11.2", {"start": v(1765, -3057.07) * mm, "end": v(1761.27, -3050.61) * mm, "construction": true});
            skLineSegment(sketch, "E33.12.0", {"start": v(2363.52, -2621.96) * mm, "end": v(2854.65, -2076.5) * mm});
            skLineSegment(sketch, "E33.12.1", {"start": v(2852.6, -2072.53) * mm, "end": v(2359.35, -2620.33) * mm});
            skLineSegment(sketch, "E33.12.2", {"start": v(2362.03, -2623.3) * mm, "end": v(2357.04, -2617.76) * mm, "construction": true});
            skLineSegment(sketch, "E33.13.0", {"start": v(2857, -2073.26) * mm, "end": v(3224, -1437.6) * mm});
            skLineSegment(sketch, "E33.13.1", {"start": v(3221.16, -1434.15) * mm, "end": v(2852.6, -2072.53) * mm});
            skLineSegment(sketch, "E33.13.2", {"start": v(2855.83, -2074.88) * mm, "end": v(2849.8, -2070.5) * mm, "construction": true});
            skLineSegment(sketch, "E33.14.0", {"start": v(3225.63, -1433.95) * mm, "end": v(3452.45, -735.88) * mm});
            skLineSegment(sketch, "E33.14.1", {"start": v(3448.95, -733.1) * mm, "end": v(3221.16, -1434.15) * mm});
            skLineSegment(sketch, "E33.14.2", {"start": v(3224.82, -1435.78) * mm, "end": v(3218, -1432.75) * mm, "construction": true});
            skLineSegment(sketch, "E33.15.0", {"start": v(3453.28, -731.97) * mm, "end": v(3530, -2) * mm});
            skLineSegment(sketch, "E33.15.1", {"start": v(3526, 0) * mm, "end": v(3448.95, -733.1) * mm});
            skLineSegment(sketch, "E33.15.2", {"start": v(3452.86, -733.93) * mm, "end": v(3445.57, -732.38) * mm, "construction": true});
            skLineSegment(sketch, "E33.16.0", {"start": v(3530, 2) * mm, "end": v(3453.28, 731.97) * mm});
            skLineSegment(sketch, "E33.16.1", {"start": v(3448.95, 733.1) * mm, "end": v(3526, 0) * mm});
            skLineSegment(sketch, "E33.16.2", {"start": v(3530, 0) * mm, "end": v(3522.54, 0) * mm, "construction": true});
            skLineSegment(sketch, "E33.17.0", {"start": v(3452.45, 735.88) * mm, "end": v(3225.63, 1433.95) * mm});
            skLineSegment(sketch, "E33.17.1", {"start": v(3221.16, 1434.15) * mm, "end": v(3448.95, 733.1) * mm});
            skLineSegment(sketch, "E33.17.2", {"start": v(3452.86, 733.93) * mm, "end": v(3445.57, 732.38) * mm, "construction": true});
            skLineSegment(sketch, "E33.18.0", {"start": v(3224, 1437.6) * mm, "end": v(2857, 2073.26) * mm});
            skLineSegment(sketch, "E33.18.1", {"start": v(2852.6, 2072.53) * mm, "end": v(3221.16, 1434.15) * mm});
            skLineSegment(sketch, "E33.18.2", {"start": v(3224.82, 1435.78) * mm, "end": v(3218, 1432.75) * mm, "construction": true});
            skLineSegment(sketch, "E33.19.0", {"start": v(2854.65, 2076.5) * mm, "end": v(2363.52, 2621.96) * mm});
            skLineSegment(sketch, "E33.19.1", {"start": v(2359.35, 2620.33) * mm, "end": v(2852.6, 2072.53) * mm});
            skLineSegment(sketch, "E33.19.2", {"start": v(2855.83, 2074.88) * mm, "end": v(2849.8, 2070.5) * mm, "construction": true});
            skLineSegment(sketch, "E33.20.0", {"start": v(2360.54, 2624.64) * mm, "end": v(1766.73, 3056.07) * mm});
            skLineSegment(sketch, "E33.20.1", {"start": v(1763, 3053.6) * mm, "end": v(2359.35, 2620.33) * mm});
            skLineSegment(sketch, "E33.20.2", {"start": v(2362.03, 2623.3) * mm, "end": v(2357.04, 2617.76) * mm, "construction": true});
            skLineSegment(sketch, "E33.21.0", {"start": v(1763.27, 3058.07) * mm, "end": v(1092.73, 3356.61) * mm});
            skLineSegment(sketch, "E33.21.1", {"start": v(1089.6, 3353.43) * mm, "end": v(1763, 3053.6) * mm});
            skLineSegment(sketch, "E33.21.2", {"start": v(1765, 3057.07) * mm, "end": v(1761.27, 3050.61) * mm, "construction": true});
            skLineSegment(sketch, "E33.22.0", {"start": v(1088.93, 3357.85) * mm, "end": v(370.97, 3510.45) * mm});
            skLineSegment(sketch, "E33.22.1", {"start": v(368.57, 3506.68) * mm, "end": v(1089.6, 3353.43) * mm});
            skLineSegment(sketch, "E33.22.2", {"start": v(1090.83, 3357.23) * mm, "end": v(1088.53, 3350.14) * mm, "construction": true});
            skLineSegment(sketch, "E33.23.0", {"start": v(367, 3510.87) * mm, "end": v(-367, 3510.87) * mm});
            skLineSegment(sketch, "E33.23.1", {"start": v(-368.57, 3506.68) * mm, "end": v(368.57, 3506.68) * mm});
            skLineSegment(sketch, "E33.23.2", {"start": v(368.99, 3510.66) * mm, "end": v(368.2, 3503.25) * mm, "construction": true});
            skLineSegment(sketch, "E33.24.0", {"start": v(-370.97, 3510.45) * mm, "end": v(-1088.93, 3357.85) * mm});
            skLineSegment(sketch, "E33.24.1", {"start": v(-1089.6, 3353.43) * mm, "end": v(-368.57, 3506.68) * mm});
            skLineSegment(sketch, "E33.24.2", {"start": v(-368.99, 3510.66) * mm, "end": v(-368.2, 3503.25) * mm, "construction": true});
            skLineSegment(sketch, "E33.25.0", {"start": v(-1092.73, 3356.61) * mm, "end": v(-1763.27, 3058.07) * mm});
            skLineSegment(sketch, "E33.25.1", {"start": v(-1763, 3053.6) * mm, "end": v(-1089.6, 3353.43) * mm});
            skLineSegment(sketch, "E33.25.2", {"start": v(-1090.83, 3357.23) * mm, "end": v(-1088.53, 3350.14) * mm, "construction": true});
            skLineSegment(sketch, "E33.26.0", {"start": v(-1766.73, 3056.07) * mm, "end": v(-2360.54, 2624.64) * mm});
            skLineSegment(sketch, "E33.26.1", {"start": v(-2359.35, 2620.33) * mm, "end": v(-1763, 3053.6) * mm});
            skLineSegment(sketch, "E33.26.2", {"start": v(-1765, 3057.07) * mm, "end": v(-1761.27, 3050.61) * mm, "construction": true});
            skLineSegment(sketch, "E33.27.0", {"start": v(-2363.52, 2621.96) * mm, "end": v(-2854.65, 2076.5) * mm});
            skLineSegment(sketch, "E33.27.1", {"start": v(-2852.6, 2072.53) * mm, "end": v(-2359.35, 2620.33) * mm});
            skLineSegment(sketch, "E33.27.2", {"start": v(-2362.03, 2623.3) * mm, "end": v(-2357.04, 2617.76) * mm, "construction": true});
            skLineSegment(sketch, "E33.28.0", {"start": v(-2857, 2073.26) * mm, "end": v(-3224, 1437.6) * mm});
            skLineSegment(sketch, "E33.28.1", {"start": v(-3221.16, 1434.15) * mm, "end": v(-2852.6, 2072.53) * mm});
            skLineSegment(sketch, "E33.28.2", {"start": v(-2855.83, 2074.88) * mm, "end": v(-2849.8, 2070.5) * mm, "construction": true});
            skLineSegment(sketch, "E33.29.0", {"start": v(-3225.63, 1433.95) * mm, "end": v(-3452.45, 735.88) * mm});
            skLineSegment(sketch, "E33.29.1", {"start": v(-3448.95, 733.1) * mm, "end": v(-3221.16, 1434.15) * mm});
            skLineSegment(sketch, "E33.29.2", {"start": v(-3224.82, 1435.78) * mm, "end": v(-3218, 1432.75) * mm, "construction": true});
            skSolve(sketch);
        }
        {
            var Q0;
            Q0 = qSketchRegion(id + "F3", true);
            var Q1;
            Q1=sQuery(id+"F3.wireOp",EDGE,"E17");
            extrude(context, id + "F4", {"entities" : qUnion([Q0]), "surfaceEntities" : qUnion([Q1]), "depth" : 5 * mm, "offsetDistance" : 25 * mm});
        }
        {
            var Q0;
            Q0 = qSketchRegion(id + "F0", true);
            extrude(context, id + "F5", {"entities" : qUnion([Q0]), "oppositeDirection" : true, "depth" : 5 * mm, "offsetDistance" : 25 * mm});
        }
        {
            var Q0;
            Q0=qCreatedBy(makeId("Front.planeOp"),FACE);
            cPlane(context, id + "F6", {"entities" : qUnion([Q0]), "cplaneType" : CPlaneType.OFFSET, "offset" : 180 * mm, "width" : 150 * mm, "height" : 150 * mm});
        }
        {
            var Q0;
            Q0=qCreatedBy(id+"F6.planeOp",FACE);
            var sketch = newSketch(context, id + "F7", { "sketchPlane" : qUnion([Q0])});
            skPoint(sketch, "E34", {"position": v(-3700, 0) * mm});
            skPoint(sketch, "E35", {"position": v(-3690, 0) * mm});
            skArc(sketch, "E36", {"start": v(-3690, 0) * mm, "mid": v(-2609.22, 2609.22) * mm, "end": v(0, 3690) * mm});
            skArc(sketch, "E37", {"start": v(0, 3690) * mm, "mid": v(-3690, 0) * mm, "end": v(0, -3690) * mm});
            skLineSegment(sketch, "E38", {"start": v(0, -3690) * mm, "end": v(0, -3520) * mm});
            skArc(sketch, "E39", {"start": v(0, -3520) * mm, "mid": v(-3520, 0) * mm, "end": v(0, 3520) * mm});
            skLineSegment(sketch, "E40", {"start": v(0, 3690) * mm, "end": v(0, 3520) * mm});
            skPoint(sketch, "E41", {"position": v(0, 3695) * mm});
            skLineSegment(sketch, "E42", {"start": v(0, 3690) * mm, "end": v(0, 3695) * mm});
            skArc(sketch, "E43", {"start": v(0, 3695) * mm, "mid": v(-3695, 0) * mm, "end": v(0, -3695) * mm});
            skLineSegment(sketch, "E44", {"start": v(0, -3695) * mm, "end": v(0, -3690) * mm});
            skPoint(sketch, "E45", {"position": v(-3690, 3690) * mm});
            skLineSegment(sketch, "E46", {"start": v(-3690, 3690) * mm, "end": v(-1701.3, 3690) * mm});
            skLineSegment(sketch, "E47", {"start": v(-1701.3, 3690) * mm, "end": v(-1701.3, 3280.03) * mm});
            skLineSegment(sketch, "E48", {"start": v(-1039.76, 3936.6) * mm, "end": v(-840.27, 3837.12) * mm});
            skLineSegment(sketch, "E49", {"start": v(0, 3980.68) * mm, "end": v(-319.47, 4140) * mm});
            skLineSegment(sketch, "E50", {"start": v(0, 3695) * mm, "end": v(0, 3980.68) * mm});
            skLineSegment(sketch, "E51", {"start": v(-1701.3, 3690) * mm, "end": v(-840.27, 3837.12) * mm, "construction": true});
            skLineSegment(sketch, "E52", {"start": v(-1058.52, 3799.83) * mm, "end": v(214.58, 4017.35) * mm, "construction": true});
            skPoint(sketch, "E53", {"position": v(-3690, 3680) * mm});
            skLineSegment(sketch, "E54", {"start": v(-3690, 3690) * mm, "end": v(-3690, 3680) * mm});
            skLineSegment(sketch, "E55", {"start": v(-3690, 3680) * mm, "end": v(-1711.3, 3680) * mm});
            skLineSegment(sketch, "E56", {"start": v(-1711.3, 3680) * mm, "end": v(-1711.3, 3274.82) * mm});
            skLineSegment(sketch, "E57", {"start": v(-1039.76, 3936.6) * mm, "end": v(-1044.22, 3927.65) * mm});
            skLineSegment(sketch, "E58", {"start": v(-1044.22, 3927.65) * mm, "end": v(-850.27, 3830.93) * mm});
            skLineSegment(sketch, "E59", {"start": v(-850.27, 3830.93) * mm, "end": v(-850.27, 3595.84) * mm});
            skLineSegment(sketch, "E60", {"start": v(-319.47, 4140) * mm, "end": v(-323.93, 4131.05) * mm});
            skLineSegment(sketch, "E61", {"start": v(-323.93, 4131.05) * mm, "end": v(-10, 3974.5) * mm});
            skLineSegment(sketch, "E62", {"start": v(-10, 3974.5) * mm, "end": v(-10, 3694.99) * mm});
            skLineSegment(sketch, "E63", {"start": v(-319.47, 4140) * mm, "end": v(-3690, 4140) * mm});
            skLineSegment(sketch, "E64", {"start": v(-3690, 4140) * mm, "end": v(-3690, 3690) * mm});
            skLineSegment(sketch, "E65", {"start": v(-1701.3, 3280.03) * mm, "end": v(-1703.2, 3273.4) * mm});
            skLineSegment(sketch, "E66", {"start": v(-840.27, 3837.12) * mm, "end": v(-840.27, 3598.2) * mm});
            skLineSegment(sketch, "E67", {"start": v(-10, 3694.99) * mm, "end": v(-10, 3689.99) * mm});
            skSolve(sketch);
        }
        {
            var Q0;
            Q0=qCreatedBy(makeId("Front.planeOp"),FACE);
            cPlane(context, id + "F8", {"entities" : qUnion([Q0]), "cplaneType" : CPlaneType.OFFSET, "offset" : 10 * mm, "oppositeDirection" : true, "width" : 150 * mm, "height" : 150 * mm});
        }
        {
            var Q0;
            Q0=qCreatedBy(id+"F8.planeOp",FACE);
            var sketch = newSketch(context, id + "F9", { "sketchPlane" : qUnion([Q0])});
            skPoint(sketch, "E68", {"position": v(-3705, 0) * mm});
            skPoint(sketch, "E69", {"position": v(-3695, 0) * mm});
            skArc(sketch, "E70", {"start": v(-3695, 0) * mm, "mid": v(-2612.76, 2612.76) * mm, "end": v(0, 3695) * mm});
            skArc(sketch, "E71", {"start": v(0, 3695) * mm, "mid": v(-3695, 0) * mm, "end": v(0, -3695) * mm});
            skLineSegment(sketch, "E72", {"start": v(0, -3695) * mm, "end": v(0, -3525) * mm});
            skArc(sketch, "E73", {"start": v(0, -3525) * mm, "mid": v(-3525, 0) * mm, "end": v(0, 3525) * mm});
            skLineSegment(sketch, "E74", {"start": v(0, 3695) * mm, "end": v(0, 3525) * mm});
            skPoint(sketch, "E75", {"position": v(0, 3695) * mm});
            skLineSegment(sketch, "E76", {"start": v(0, 3690) * mm, "end": v(0, 3695) * mm});
            skPoint(sketch, "E77", {"position": v(-3690, 3690) * mm});
            skLineSegment(sketch, "E78", {"start": v(-3690, 3690) * mm, "end": v(-1701.3, 3690) * mm});
            skLineSegment(sketch, "E79", {"start": v(-1701.3, 3690) * mm, "end": v(-1701.3, 3280.03) * mm});
            skLineSegment(sketch, "E80", {"start": v(-1039.76, 3936.6) * mm, "end": v(-840.27, 3837.12) * mm});
            skLineSegment(sketch, "E81", {"start": v(-840.27, 3837.12) * mm, "end": v(-840.27, 3593.06) * mm});
            skLineSegment(sketch, "E82", {"start": v(0, 3980.68) * mm, "end": v(-319.47, 4140) * mm});
            skLineSegment(sketch, "E83", {"start": v(0, 3695) * mm, "end": v(0, 3980.68) * mm});
            skLineSegment(sketch, "E84", {"start": v(-1701.3, 3690) * mm, "end": v(-840.27, 3837.12) * mm, "construction": true});
            skLineSegment(sketch, "E85", {"start": v(-1058.52, 3799.83) * mm, "end": v(214.58, 4017.35) * mm, "construction": true});
            skPoint(sketch, "E86", {"position": v(-3690, 3680) * mm});
            skLineSegment(sketch, "E87", {"start": v(-3690, 3690) * mm, "end": v(-3690, 3680) * mm});
            skLineSegment(sketch, "E88", {"start": v(-3690, 3680) * mm, "end": v(-1711.3, 3680) * mm});
            skLineSegment(sketch, "E89", {"start": v(-1711.3, 3680) * mm, "end": v(-1711.3, 3274.82) * mm});
            skLineSegment(sketch, "E90", {"start": v(-1039.76, 3936.6) * mm, "end": v(-1044.22, 3927.65) * mm});
            skLineSegment(sketch, "E91", {"start": v(-1044.22, 3927.65) * mm, "end": v(-850.27, 3830.93) * mm});
            skLineSegment(sketch, "E92", {"start": v(-850.27, 3830.93) * mm, "end": v(-850.27, 3595.84) * mm});
            skLineSegment(sketch, "E93", {"start": v(-319.47, 4140) * mm, "end": v(-323.93, 4131.05) * mm});
            skLineSegment(sketch, "E94", {"start": v(-323.93, 4131.05) * mm, "end": v(-10, 3974.5) * mm});
            skLineSegment(sketch, "E95", {"start": v(-10, 3974.5) * mm, "end": v(-10, 3694.99) * mm});
            skLineSegment(sketch, "E96", {"start": v(-319.47, 4140) * mm, "end": v(-3690, 4140) * mm});
            skLineSegment(sketch, "E97", {"start": v(-3690, 4140) * mm, "end": v(-3690, 3690) * mm});
            skSolve(sketch);
        }
        {
            var Q0;
            {var subQ0=sQuery(id+"F7.wireOp",EDGE,"E38");Q0=makeQuery(id+"F7.imprint","IMPRINT",FACE,{"disambiguationData":[TD([[makeQuery(id+"F7.imprint","IMPRINT",EDGE,{"derivedFrom":subQ0}),1.0]])]});}
            var Q1;
            Q1=makeQuery(id+"F7.imprint","IMPRINT",FACE,{"disambiguationData":[TD([[makeQuery(id+"F7.imprint","IMPRINT",EDGE,{"derivedFrom":sQuery(id+"F7.wireOp",EDGE,"E49")}),1.0]])]});
            var Q2;
            Q2=makeQuery(id+"F7.imprint","IMPRINT",FACE,{"disambiguationData":[TD([[makeQuery(id+"F7.imprint","IMPRINT",EDGE,{"derivedFrom":sQuery(id+"F7.wireOp",EDGE,"E46")}),-1.0]])]});
            var Q3;
            {var subQ4=sQuery(id+"F7.wireOp",EDGE,"E42");Q3=makeQuery(id+"F7.imprint","IMPRINT",FACE,{"disambiguationData":[TD([[makeQuery(id+"F7.imprint","IMPRINT",EDGE,{"derivedFrom":subQ4}),1.0]])]});}
            var Q4;
            {var subQ5=sQuery(id+"F7.wireOp",EDGE,"E44");Q4=makeQuery(id+"F7.imprint","IMPRINT",FACE,{"disambiguationData":[TD([[makeQuery(id+"F7.imprint","IMPRINT",EDGE,{"derivedFrom":subQ5}),1.0]])]});}
            var Q5;
            {var subQ1=sQuery(id+"F7.wireOp",EDGE,"E48");Q5=makeQuery(id+"F7.imprint","IMPRINT",FACE,{"disambiguationData":[TD([[makeQuery(id+"F7.imprint","IMPRINT",EDGE,{"derivedFrom":subQ1}),-1.0]])]});}
            var Q6;
            Q6=makeQuery(id+"F7.imprint","IMPRINT",FACE,{"disambiguationData":[TD([[makeQuery(id+"F7.imprint","IMPRINT",EDGE,{"derivedFrom":sQuery(id+"F7.wireOp",EDGE,"E46")}),1.0]])]});
            var Q7;
            {var subQ4=sQuery(id+"F7.wireOp",EDGE,"E65");Q7=makeQuery(id+"F7.imprint","IMPRINT",FACE,{"disambiguationData":[TD([[makeQuery(id+"F7.imprint","IMPRINT",EDGE,{"derivedFrom":subQ4}),1.0]])]});}
            var Q8;
            Q8=makeQuery(id+"F9.imprint","IMPRINT",FACE,{"disambiguationData":[TD([[makeQuery(id+"F9.imprint","IMPRINT",EDGE,{"derivedFrom":sQuery(id+"F9.wireOp",EDGE,"E78")}),1.0]])]});
            var Q9;
            {var subQ1=sQuery(id+"F9.wireOp",EDGE,"E80");Q9=makeQuery(id+"F9.imprint","IMPRINT",FACE,{"disambiguationData":[TD([[makeQuery(id+"F9.imprint","IMPRINT",EDGE,{"derivedFrom":subQ1}),-1.0]])]});}
            extrude(context, id + "F10", {"entities" : qUnion([Q0, Q1, Q2, Q3, Q4, Q5, Q6, Q7, Q8, Q9]), "operationType" : NewBodyOperationType.ADD, "depth" : 5 * mm, "offsetDistance" : 25 * mm});
        }
        {
            var Q0;
            Q0=makeQuery(id+"FDxFbJvoRVe9rJm_5.opExtrude","SWEPT_FACE",FACE,{"disambiguationData":[OSD([sQuery(id+"F7.wireOp",EDGE,"E44")])]});
            var Q1;
            Q1=makeQuery(id+"F10.opExtrude","SWEPT_FACE",FACE,{"disambiguationData":[OSD([sQuery(id+"F7.wireOp",EDGE,"E38"),sQuery(id+"F7.wireOp",EDGE,"E44")])]});
            var Q2;
            Q2=makeQuery(id+"FtzKbi7jnpRppUM_3.opExtrude","SWEPT_FACE",FACE,{"disambiguationData":[OSD([sQuery(id+"F9.wireOp",EDGE,"E72")])]});
            extrude(context, id + "F11", {"entities" : qUnion([Q0, Q1, Q2]), "depth" : 700 * mm, "offsetDistance" : 25 * mm});
        }
        {
            var Q0;
            {var subQ0=sQuery(id+"F7.wireOp",EDGE,"E44");Q0=makeQuery(id+"F7.imprint","IMPRINT",FACE,{"disambiguationData":[TD([[makeQuery(id+"F7.imprint","IMPRINT",EDGE,{"derivedFrom":subQ0}),1.0]])]});}
            var Q1;
            Q1=makeQuery(id+"F7.imprint","IMPRINT",FACE,{"disambiguationData":[TD([[makeQuery(id+"F7.imprint","IMPRINT",EDGE,{"derivedFrom":sQuery(id+"F7.wireOp",EDGE,"E46")}),-1.0]])]});
            var Q2;
            Q2=makeQuery(id+"F7.imprint","IMPRINT",FACE,{"disambiguationData":[TD([[makeQuery(id+"F7.imprint","IMPRINT",EDGE,{"derivedFrom":sQuery(id+"F7.wireOp",EDGE,"E48")}),-1.0]])]});
            var Q3;
            {var subQ0=sQuery(id+"F7.wireOp",EDGE,"E42");Q3=makeQuery(id+"F7.imprint","IMPRINT",FACE,{"disambiguationData":[TD([[makeQuery(id+"F7.imprint","IMPRINT",EDGE,{"derivedFrom":subQ0}),1.0]])]});}
            var Q4;
            Q4=makeQuery(id+"F7.imprint","IMPRINT",FACE,{"disambiguationData":[TD([[makeQuery(id+"F7.imprint","IMPRINT",EDGE,{"derivedFrom":sQuery(id+"F7.wireOp",EDGE,"E49")}),1.0]])]});
            extrude(context, id + "F12", {"entities" : qUnion([Q0, Q1, Q2, Q3, Q4]), "operationType" : NewBodyOperationType.ADD, "oppositeDirection" : true, "depth" : 190 * mm, "offsetDistance" : 25 * mm});
        }
    });
